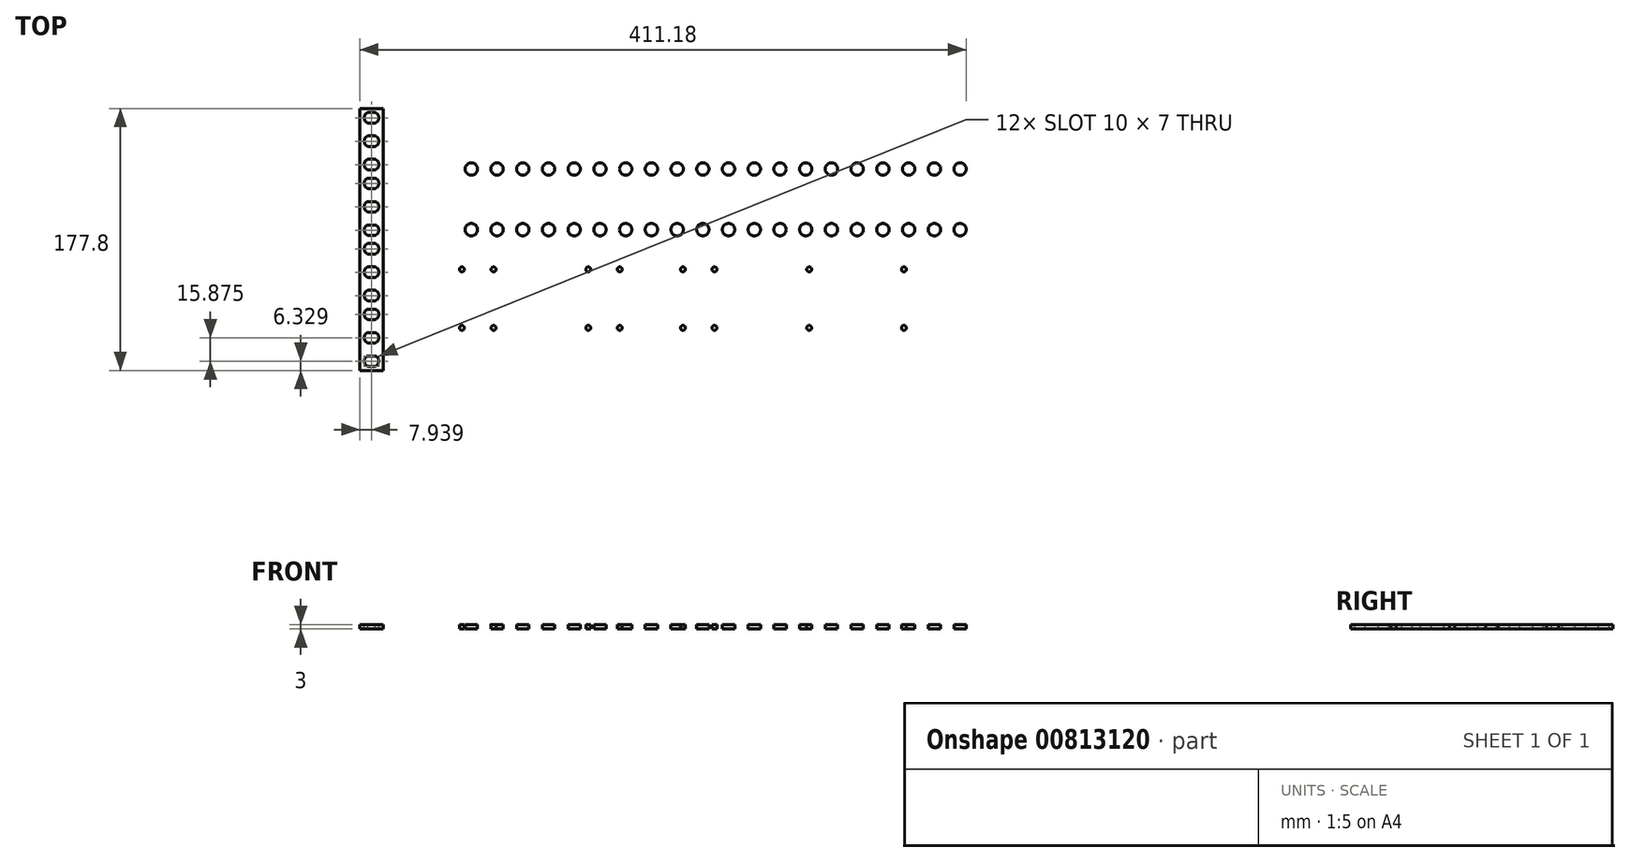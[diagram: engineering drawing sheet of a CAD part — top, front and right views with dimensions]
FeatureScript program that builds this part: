
annotation { "Feature Type Name" : "Feature", "Feature Type Description" : "" }
export const myFeature = defineFeature(function(context is Context, id is Id, definition is map)
    precondition{}
    {
        {
            var Q0;
            Q0=qCreatedBy(makeId("Top.planeOp"),FACE);
            var sketch = newSketch(context, id + "F0", { "sketchPlane" : qUnion([Q0])});
            skLineSegment(sketch, "E0.bottom", {"start": v(-66.95, 141.25) * mm, "end": v(415.65, 141.25) * mm});
            skLineSegment(sketch, "E0.top", {"start": v(-66.95, -36.55) * mm, "end": v(415.65, -36.55) * mm});
            skLineSegment(sketch, "E0.left", {"start": v(-66.95, 141.25) * mm, "end": v(-66.95, -36.55) * mm});
            skLineSegment(sketch, "E0.right", {"start": v(415.65, 141.25) * mm, "end": v(415.65, -36.55) * mm});
            skSolve(sketch);
        }
        {
            var Q0;
            Q0=makeQuery(id+"F0.imprint","IMPRINT",FACE,{"disambiguationData":[TD([[makeQuery(id+"F0.imprint","IMPRINT",EDGE,{"derivedFrom":sQuery(id+"F0.wireOp",EDGE,"E0.bottom")}),-1.0]])]});
            extrude(context, id + "F1", {"entities" : qUnion([Q0]), "depth" : 3 * mm, "offsetDistance" : 25 * mm});
        }
        {
            var Q0;
            Q0=makeQuery(id+"F1.opExtrude","CAP_FACE",FACE,{"disambiguationData":[OSD([sQuery(id+"F0.wireOp",EDGE,"E0.bottom"),sQuery(id+"F0.wireOp",EDGE,"E0.top"),sQuery(id+"F0.wireOp",EDGE,"E0.left"),sQuery(id+"F0.wireOp",EDGE,"E0.right")])],"isStart":false});
            var sketch = newSketch(context, id + "F2", { "sketchPlane" : qUnion([Q0])});
            skPoint(sketch, "E1", {"position": v(-59.01, 134.9) * mm});
            skPoint(sketch, "E2", {"position": v(-59.01, 119.02) * mm});
            skPoint(sketch, "E3", {"position": v(-59.01, 103.15) * mm});
            skPoint(sketch, "E4", {"position": v(8.67, 120.69) * mm});
            skPoint(sketch, "E5", {"position": v(26.1, 120.69) * mm});
            skPoint(sketch, "E6", {"position": v(43.55, 120.69) * mm});
            skPoint(sketch, "E7", {"position": v(60.99, 120.69) * mm});
            skPoint(sketch, "E8", {"position": v(78.43, 120.69) * mm});
            skPoint(sketch, "E9", {"position": v(95.87, 120.69) * mm});
            skPoint(sketch, "E10", {"position": v(113.3, 120.69) * mm});
            skPoint(sketch, "E11", {"position": v(130.75, 120.69) * mm});
            skPoint(sketch, "E12", {"position": v(148.19, 120.69) * mm});
            skPoint(sketch, "E13", {"position": v(165.63, 120.69) * mm});
            skPoint(sketch, "E14", {"position": v(183.07, 120.69) * mm});
            skPoint(sketch, "E15", {"position": v(200.5, 120.69) * mm});
            skPoint(sketch, "E16", {"position": v(217.95, 120.69) * mm});
            skPoint(sketch, "E17", {"position": v(235.39, 120.69) * mm});
            skPoint(sketch, "E18", {"position": v(252.83, 120.69) * mm});
            skPoint(sketch, "E19", {"position": v(270.27, 120.69) * mm});
            skPoint(sketch, "E20", {"position": v(287.7, 120.69) * mm});
            skPoint(sketch, "E21", {"position": v(305.15, 120.69) * mm});
            skPoint(sketch, "E22", {"position": v(322.59, 120.69) * mm});
            skPoint(sketch, "E23", {"position": v(340.03, 120.69) * mm});
            skCircle(sketch, "E24", {"center": v(8.67, 120.69) * mm, "radius": 4.2 * mm});
            skCircle(sketch, "E25", {"center": v(26.1, 120.69) * mm, "radius": 4.2 * mm});
            skCircle(sketch, "E26", {"center": v(43.55, 120.69) * mm, "radius": 4.2 * mm});
            skCircle(sketch, "E27", {"center": v(60.99, 120.69) * mm, "radius": 4.2 * mm});
            skCircle(sketch, "E28", {"center": v(78.43, 120.69) * mm, "radius": 4.2 * mm});
            skCircle(sketch, "E29", {"center": v(95.87, 120.69) * mm, "radius": 4.2 * mm});
            skCircle(sketch, "E30", {"center": v(113.3, 120.69) * mm, "radius": 4.2 * mm});
            skCircle(sketch, "E31", {"center": v(130.75, 120.69) * mm, "radius": 4.2 * mm});
            skCircle(sketch, "E32", {"center": v(148.19, 120.69) * mm, "radius": 4.2 * mm});
            skCircle(sketch, "E33", {"center": v(165.63, 120.69) * mm, "radius": 4.2 * mm});
            skCircle(sketch, "E34", {"center": v(183.07, 120.69) * mm, "radius": 4.2 * mm});
            skCircle(sketch, "E35", {"center": v(200.5, 120.69) * mm, "radius": 4.2 * mm});
            skCircle(sketch, "E36", {"center": v(217.95, 120.69) * mm, "radius": 4.2 * mm});
            skCircle(sketch, "E37", {"center": v(235.39, 120.69) * mm, "radius": 4.2 * mm});
            skCircle(sketch, "E38", {"center": v(252.83, 120.69) * mm, "radius": 4.2 * mm});
            skCircle(sketch, "E39", {"center": v(270.27, 120.69) * mm, "radius": 4.2 * mm});
            skCircle(sketch, "E40", {"center": v(287.7, 120.69) * mm, "radius": 4.2 * mm});
            skCircle(sketch, "E41", {"center": v(305.15, 120.69) * mm, "radius": 4.2 * mm});
            skCircle(sketch, "E42", {"center": v(340.03, 120.69) * mm, "radius": 4.2 * mm});
            skCircle(sketch, "E43", {"center": v(322.59, 120.69) * mm, "radius": 4.2 * mm});
            skLineSegment(sketch, "E44.MirrorCS", {"start": v(-59.01, 106.66) * mm, "end": v(-56.51, 106.66) * mm});
            skLineSegment(sketch, "E45.MirrorCS", {"start": v(-59.01, 106.66) * mm, "end": v(-61.51, 106.66) * mm});
            skLineSegment(sketch, "E46.MirrorCS", {"start": v(-59.01, 122.54) * mm, "end": v(-61.51, 122.54) * mm});
            skLineSegment(sketch, "E47.MirrorCS", {"start": v(-59.01, 115.54) * mm, "end": v(-61.51, 115.54) * mm});
            skLineSegment(sketch, "E48.MirrorCS", {"start": v(-59.01, 131.41) * mm, "end": v(-56.51, 131.41) * mm});
            skLineSegment(sketch, "E49.MirrorCS", {"start": v(-59.01, 99.66) * mm, "end": v(-61.51, 99.66) * mm});
            skLineSegment(sketch, "E50.MirrorCS", {"start": v(-59.01, 131.41) * mm, "end": v(-61.51, 131.41) * mm});
            skLineSegment(sketch, "E51.MirrorCS", {"start": v(-59.01, 138.41) * mm, "end": v(-56.51, 138.41) * mm});
            skLineSegment(sketch, "E52.MirrorCS", {"start": v(-59.01, 115.54) * mm, "end": v(-56.51, 115.54) * mm});
            skLineSegment(sketch, "E53.MirrorCS", {"start": v(-59.01, 99.66) * mm, "end": v(-56.51, 99.66) * mm});
            skLineSegment(sketch, "E54.MirrorCS", {"start": v(-59.01, 138.41) * mm, "end": v(-61.51, 138.41) * mm});
            skLineSegment(sketch, "E55.MirrorCS", {"start": v(-59.01, 122.54) * mm, "end": v(-56.51, 122.54) * mm});
            skArc(sketch, "E56.MirrorCS", {"start": v(-61.51, 122.54) * mm, "mid": v(-64.01, 119.04) * mm, "end": v(-61.51, 115.54) * mm});
            skArc(sketch, "E57.MirrorCS", {"start": v(-61.51, 99.66) * mm, "mid": v(-64.01, 103.16) * mm, "end": v(-61.51, 106.66) * mm});
            skArc(sketch, "E58.MirrorCS", {"start": v(-56.51, 106.66) * mm, "mid": v(-54.01, 103.16) * mm, "end": v(-56.51, 99.66) * mm});
            skPoint(sketch, "E59.MirrorP", {"position": v(-64.01, 103.15) * mm});
            skArc(sketch, "E60.MirrorCS", {"start": v(-61.51, 131.41) * mm, "mid": v(-64.01, 134.91) * mm, "end": v(-61.51, 138.41) * mm});
            skArc(sketch, "E61.MirrorCS", {"start": v(-56.51, 115.54) * mm, "mid": v(-54.01, 119.04) * mm, "end": v(-56.51, 122.54) * mm});
            skArc(sketch, "E62.MirrorCS", {"start": v(-56.51, 138.41) * mm, "mid": v(-54.01, 134.91) * mm, "end": v(-56.51, 131.41) * mm});
            skPoint(sketch, "E63", {"position": v(-40.48, 32.03) * mm});
            skPoint(sketch, "E64", {"position": v(-19.08, 32.03) * mm});
            skPoint(sketch, "E65", {"position": v(-19.08, -7.67) * mm});
            skCircle(sketch, "E66", {"center": v(-40.48, 32.03) * mm, "radius": 1.65 * mm});
            skCircle(sketch, "E67", {"center": v(-19.08, 32.03) * mm, "radius": 1.65 * mm});
            skCircle(sketch, "E68", {"center": v(-19.08, -7.67) * mm, "radius": 1.65 * mm});
            skCircle(sketch, "E69.MirrorC", {"center": v(2.32, 32.03) * mm, "radius": 1.65 * mm});
            skCircle(sketch, "E70.MirrorC", {"center": v(2.32, -7.67) * mm, "radius": 1.65 * mm});
            skCircle(sketch, "E71.MirrorC", {"center": v(23.72, 32.03) * mm, "radius": 1.65 * mm});
            skCircle(sketch, "E72.MirrorC", {"center": v(23.72, -7.67) * mm, "radius": 1.65 * mm});
            skPoint(sketch, "E73.MirrorP", {"position": v(45.12, 32.03) * mm});
            skCircle(sketch, "E74.MirrorC", {"center": v(45.12, -7.67) * mm, "radius": 1.65 * mm});
            skCircle(sketch, "E75.MirrorC", {"center": v(45.12, 32.03) * mm, "radius": 1.65 * mm});
            skPoint(sketch, "E76.MirrorP", {"position": v(66.52, -7.67) * mm});
            skPoint(sketch, "E77.MirrorP", {"position": v(66.52, 32.03) * mm});
            skCircle(sketch, "E78.MirrorC", {"center": v(66.52, -7.67) * mm, "radius": 1.65 * mm});
            skCircle(sketch, "E79.MirrorC", {"center": v(66.52, 32.03) * mm, "radius": 1.65 * mm});
            skPoint(sketch, "E80.MirrorP", {"position": v(87.92, -7.67) * mm});
            skCircle(sketch, "E81.MirrorC", {"center": v(87.92, 32.03) * mm, "radius": 1.65 * mm});
            skCircle(sketch, "E82.MirrorC", {"center": v(87.92, -7.67) * mm, "radius": 1.65 * mm});
            skCircle(sketch, "E83.MirrorC", {"center": v(109.32, 32.03) * mm, "radius": 1.65 * mm});
            skCircle(sketch, "E84.MirrorC", {"center": v(109.32, -7.67) * mm, "radius": 1.65 * mm});
            skCircle(sketch, "E85.MirrorC", {"center": v(194.92, -7.67) * mm, "radius": 1.65 * mm});
            skCircle(sketch, "E86.MirrorC", {"center": v(194.92, 32.03) * mm, "radius": 1.65 * mm});
            skCircle(sketch, "E87.MirrorC", {"center": v(152.12, -7.67) * mm, "radius": 1.65 * mm});
            skCircle(sketch, "E88.MirrorC", {"center": v(173.52, 32.03) * mm, "radius": 1.65 * mm});
            skCircle(sketch, "E89.MirrorC", {"center": v(216.32, -7.67) * mm, "radius": 1.65 * mm});
            skCircle(sketch, "E90.MirrorC", {"center": v(216.32, 32.03) * mm, "radius": 1.65 * mm});
            skCircle(sketch, "E91.MirrorC", {"center": v(173.52, -7.67) * mm, "radius": 1.65 * mm});
            skCircle(sketch, "E92.MirrorC", {"center": v(152.12, 32.03) * mm, "radius": 1.65 * mm});
            skCircle(sketch, "E93.MirrorC", {"center": v(130.72, -7.67) * mm, "radius": 1.65 * mm});
            skCircle(sketch, "E94.MirrorC", {"center": v(130.72, 32.03) * mm, "radius": 1.65 * mm});
            skCircle(sketch, "E95.MirrorC", {"center": v(280.52, 32.03) * mm, "radius": 1.65 * mm});
            skCircle(sketch, "E96.MirrorC", {"center": v(301.92, -7.67) * mm, "radius": 1.65 * mm});
            skCircle(sketch, "E97.MirrorC", {"center": v(301.92, 32.03) * mm, "radius": 1.65 * mm});
            skCircle(sketch, "E98.MirrorC", {"center": v(259.12, -7.67) * mm, "radius": 1.65 * mm});
            skCircle(sketch, "E99.MirrorC", {"center": v(237.72, 32.03) * mm, "radius": 1.65 * mm});
            skCircle(sketch, "E100.MirrorC", {"center": v(237.72, -7.67) * mm, "radius": 1.65 * mm});
            skCircle(sketch, "E101.MirrorC", {"center": v(323.32, 32.03) * mm, "radius": 1.65 * mm});
            skCircle(sketch, "E102.MirrorC", {"center": v(259.12, 32.03) * mm, "radius": 1.65 * mm});
            skCircle(sketch, "E103.MirrorC", {"center": v(280.52, -7.67) * mm, "radius": 1.65 * mm});
            skCircle(sketch, "E104.MirrorC", {"center": v(323.32, -7.67) * mm, "radius": 1.65 * mm});
            skCircle(sketch, "E105.MirrorC", {"center": v(344.72, -7.67) * mm, "radius": 1.65 * mm});
            skCircle(sketch, "E106.MirrorC", {"center": v(344.72, 32.03) * mm, "radius": 1.65 * mm});
            skCircle(sketch, "E107.MirrorC", {"center": v(364.25, 107.27) * mm, "radius": 1.65 * mm});
            skCircle(sketch, "E108.MirrorC", {"center": v(364.25, 67.57) * mm, "radius": 1.65 * mm});
            skCircle(sketch, "E109.MirrorC", {"center": v(385.65, 67.55) * mm, "radius": 1.65 * mm});
            skCircle(sketch, "E110.MirrorC", {"center": v(385.65, 107.25) * mm, "radius": 1.65 * mm});
            skCircle(sketch, "E111.MirrorC", {"center": v(-36.95, 107.25) * mm, "radius": 1.65 * mm});
            skCircle(sketch, "E112.MirrorC", {"center": v(-36.95, 67.55) * mm, "radius": 1.65 * mm});
            skCircle(sketch, "E113.MirrorC", {"center": v(-15.55, 67.55) * mm, "radius": 1.65 * mm});
            skCircle(sketch, "E114.MirrorC", {"center": v(-15.55, 107.25) * mm, "radius": 1.65 * mm});
            skPoint(sketch, "E115.MirrorP", {"position": v(26.1, 100.13) * mm});
            skPoint(sketch, "E116.MirrorP", {"position": v(8.67, 100.13) * mm});
            skPoint(sketch, "E117.MirrorP", {"position": v(340.03, 100.13) * mm});
            skCircle(sketch, "E118.MirrorC", {"center": v(183.07, 100.13) * mm, "radius": 4.2 * mm});
            skCircle(sketch, "E119.MirrorC", {"center": v(322.59, 100.13) * mm, "radius": 4.2 * mm});
            skPoint(sketch, "E120.MirrorP", {"position": v(78.43, 100.13) * mm});
            skCircle(sketch, "E121.MirrorC", {"center": v(252.83, 100.13) * mm, "radius": 4.2 * mm});
            skPoint(sketch, "E122.MirrorP", {"position": v(287.7, 100.13) * mm});
            skCircle(sketch, "E123.MirrorC", {"center": v(235.39, 100.13) * mm, "radius": 4.2 * mm});
            skPoint(sketch, "E124.MirrorP", {"position": v(43.55, 100.13) * mm});
            skCircle(sketch, "E125.MirrorC", {"center": v(60.99, 100.13) * mm, "radius": 4.2 * mm});
            skCircle(sketch, "E126.MirrorC", {"center": v(200.5, 100.13) * mm, "radius": 4.2 * mm});
            skPoint(sketch, "E127.MirrorP", {"position": v(148.19, 100.13) * mm});
            skCircle(sketch, "E128.MirrorC", {"center": v(43.55, 100.13) * mm, "radius": 4.2 * mm});
            skCircle(sketch, "E129.MirrorC", {"center": v(287.7, 100.13) * mm, "radius": 4.2 * mm});
            skCircle(sketch, "E130.MirrorC", {"center": v(165.63, 100.13) * mm, "radius": 4.2 * mm});
            skCircle(sketch, "E131.MirrorC", {"center": v(340.03, 100.13) * mm, "radius": 4.2 * mm});
            skCircle(sketch, "E132.MirrorC", {"center": v(305.15, 100.13) * mm, "radius": 4.2 * mm});
            skPoint(sketch, "E133.MirrorP", {"position": v(130.75, 100.13) * mm});
            skCircle(sketch, "E134.MirrorC", {"center": v(113.3, 100.13) * mm, "radius": 4.2 * mm});
            skPoint(sketch, "E135.MirrorP", {"position": v(270.27, 100.13) * mm});
            skPoint(sketch, "E136.MirrorP", {"position": v(217.95, 100.13) * mm});
            skCircle(sketch, "E137.MirrorC", {"center": v(8.67, 100.13) * mm, "radius": 4.2 * mm});
            skCircle(sketch, "E138.MirrorC", {"center": v(130.75, 100.13) * mm, "radius": 4.2 * mm});
            skCircle(sketch, "E139.MirrorC", {"center": v(78.43, 100.13) * mm, "radius": 4.2 * mm});
            skCircle(sketch, "E140.MirrorC", {"center": v(148.19, 100.13) * mm, "radius": 4.2 * mm});
            skCircle(sketch, "E141.MirrorC", {"center": v(26.1, 100.13) * mm, "radius": 4.2 * mm});
            skCircle(sketch, "E142.MirrorC", {"center": v(217.95, 100.13) * mm, "radius": 4.2 * mm});
            skCircle(sketch, "E143.MirrorC", {"center": v(270.27, 100.13) * mm, "radius": 4.2 * mm});
            skPoint(sketch, "E144.MirrorP", {"position": v(95.87, 100.13) * mm});
            skCircle(sketch, "E145.MirrorC", {"center": v(95.87, 100.13) * mm, "radius": 4.2 * mm});
            skCircle(sketch, "E146.MirrorC", {"center": v(8.67, 59) * mm, "radius": 4.2 * mm});
            skCircle(sketch, "E147.MirrorC", {"center": v(8.67, 79.57) * mm, "radius": 4.2 * mm});
            skCircle(sketch, "E148.MirrorC", {"center": v(26.1, 79.57) * mm, "radius": 4.2 * mm});
            skCircle(sketch, "E149.MirrorC", {"center": v(26.1, 59) * mm, "radius": 4.2 * mm});
            skCircle(sketch, "E150.MirrorC", {"center": v(270.27, 59) * mm, "radius": 4.2 * mm});
            skCircle(sketch, "E151.MirrorC", {"center": v(287.7, 79.57) * mm, "radius": 4.2 * mm});
            skCircle(sketch, "E152.MirrorC", {"center": v(148.19, 59) * mm, "radius": 4.2 * mm});
            skCircle(sketch, "E153.MirrorC", {"center": v(322.59, 79.57) * mm, "radius": 4.2 * mm});
            skCircle(sketch, "E154.MirrorC", {"center": v(43.55, 79.57) * mm, "radius": 4.2 * mm});
            skCircle(sketch, "E155.MirrorC", {"center": v(252.83, 79.57) * mm, "radius": 4.2 * mm});
            skCircle(sketch, "E156.MirrorC", {"center": v(95.87, 59) * mm, "radius": 4.2 * mm});
            skCircle(sketch, "E157.MirrorC", {"center": v(60.99, 79.57) * mm, "radius": 4.2 * mm});
            skCircle(sketch, "E158.MirrorC", {"center": v(183.07, 59) * mm, "radius": 4.2 * mm});
            skCircle(sketch, "E159.MirrorC", {"center": v(113.3, 79.57) * mm, "radius": 4.2 * mm});
            skCircle(sketch, "E160.MirrorC", {"center": v(148.19, 79.57) * mm, "radius": 4.2 * mm});
            skCircle(sketch, "E161.MirrorC", {"center": v(217.95, 79.57) * mm, "radius": 4.2 * mm});
            skCircle(sketch, "E162.MirrorC", {"center": v(200.5, 59) * mm, "radius": 4.2 * mm});
            skCircle(sketch, "E163.MirrorC", {"center": v(322.59, 59) * mm, "radius": 4.2 * mm});
            skCircle(sketch, "E164.MirrorC", {"center": v(95.87, 79.57) * mm, "radius": 4.2 * mm});
            skCircle(sketch, "E165.MirrorC", {"center": v(165.63, 79.57) * mm, "radius": 4.2 * mm});
            skCircle(sketch, "E166.MirrorC", {"center": v(78.43, 59) * mm, "radius": 4.2 * mm});
            skCircle(sketch, "E167.MirrorC", {"center": v(305.15, 79.57) * mm, "radius": 4.2 * mm});
            skCircle(sketch, "E168.MirrorC", {"center": v(60.99, 59) * mm, "radius": 4.2 * mm});
            skCircle(sketch, "E169.MirrorC", {"center": v(270.27, 79.57) * mm, "radius": 4.2 * mm});
            skCircle(sketch, "E170.MirrorC", {"center": v(113.3, 59) * mm, "radius": 4.2 * mm});
            skCircle(sketch, "E171.MirrorC", {"center": v(235.39, 59) * mm, "radius": 4.2 * mm});
            skCircle(sketch, "E172.MirrorC", {"center": v(235.39, 79.57) * mm, "radius": 4.2 * mm});
            skCircle(sketch, "E173.MirrorC", {"center": v(305.15, 59) * mm, "radius": 4.2 * mm});
            skCircle(sketch, "E174.MirrorC", {"center": v(200.5, 79.57) * mm, "radius": 4.2 * mm});
            skCircle(sketch, "E175.MirrorC", {"center": v(217.95, 59) * mm, "radius": 4.2 * mm});
            skCircle(sketch, "E176.MirrorC", {"center": v(43.55, 59) * mm, "radius": 4.2 * mm});
            skCircle(sketch, "E177.MirrorC", {"center": v(130.75, 59) * mm, "radius": 4.2 * mm});
            skCircle(sketch, "E178.MirrorC", {"center": v(340.03, 79.57) * mm, "radius": 4.2 * mm});
            skCircle(sketch, "E179.MirrorC", {"center": v(340.03, 59) * mm, "radius": 4.2 * mm});
            skCircle(sketch, "E180.MirrorC", {"center": v(78.43, 79.57) * mm, "radius": 4.2 * mm});
            skCircle(sketch, "E181.MirrorC", {"center": v(183.07, 79.57) * mm, "radius": 4.2 * mm});
            skCircle(sketch, "E182.MirrorC", {"center": v(165.63, 59) * mm, "radius": 4.2 * mm});
            skCircle(sketch, "E183.MirrorC", {"center": v(130.75, 79.57) * mm, "radius": 4.2 * mm});
            skCircle(sketch, "E184.MirrorC", {"center": v(287.7, 59) * mm, "radius": 4.2 * mm});
            skCircle(sketch, "E185.MirrorC", {"center": v(252.83, 59) * mm, "radius": 4.2 * mm});
            skLineSegment(sketch, "E186", {"start": v(-51.07, 141.25) * mm, "end": v(-51.07, -36.55) * mm});
            skLineSegment(sketch, "E187", {"start": v(-66.95, 96.8) * mm, "end": v(-51.07, 96.8) * mm});
            skLineSegment(sketch, "E188.MirrorCS", {"start": v(-59.01, 71.05) * mm, "end": v(-56.51, 71.05) * mm});
            skLineSegment(sketch, "E189.MirrorCS", {"start": v(-59.01, 93.93) * mm, "end": v(-61.51, 93.93) * mm});
            skLineSegment(sketch, "E190.MirrorCS", {"start": v(-59.01, 78.05) * mm, "end": v(-61.51, 78.05) * mm});
            skLineSegment(sketch, "E191.MirrorCS", {"start": v(-59.01, 93.93) * mm, "end": v(-56.51, 93.93) * mm});
            skLineSegment(sketch, "E192.MirrorCS", {"start": v(-59.01, 78.05) * mm, "end": v(-56.51, 78.05) * mm});
            skLineSegment(sketch, "E193.MirrorCS", {"start": v(-59.01, 71.05) * mm, "end": v(-61.51, 71.05) * mm});
            skLineSegment(sketch, "E194.MirrorCS", {"start": v(-59.01, 86.93) * mm, "end": v(-61.51, 86.93) * mm});
            skLineSegment(sketch, "E195.MirrorCS", {"start": v(-59.01, 62.18) * mm, "end": v(-56.51, 62.18) * mm});
            skLineSegment(sketch, "E196.MirrorCS", {"start": v(-59.01, 55.18) * mm, "end": v(-56.51, 55.18) * mm});
            skLineSegment(sketch, "E197.MirrorCS", {"start": v(-59.01, 55.18) * mm, "end": v(-61.51, 55.18) * mm});
            skLineSegment(sketch, "E198.MirrorCS", {"start": v(-59.01, 86.93) * mm, "end": v(-56.51, 86.93) * mm});
            skLineSegment(sketch, "E199.MirrorCS", {"start": v(-59.01, 62.18) * mm, "end": v(-61.51, 62.18) * mm});
            skArc(sketch, "E200.MirrorCS", {"start": v(-61.51, 71.05) * mm, "mid": v(-64.01, 74.55) * mm, "end": v(-61.51, 78.05) * mm});
            skPoint(sketch, "E201.MirrorP", {"position": v(-59.01, 90.45) * mm});
            skPoint(sketch, "E202.MirrorP", {"position": v(-59.01, 74.57) * mm});
            skArc(sketch, "E203.MirrorCS", {"start": v(-56.51, 78.05) * mm, "mid": v(-54.01, 74.55) * mm, "end": v(-56.51, 71.05) * mm});
            skArc(sketch, "E204.MirrorCS", {"start": v(-56.51, 55.18) * mm, "mid": v(-54.01, 58.68) * mm, "end": v(-56.51, 62.18) * mm});
            skArc(sketch, "E205.MirrorCS", {"start": v(-61.51, 62.18) * mm, "mid": v(-64.01, 58.68) * mm, "end": v(-61.51, 55.18) * mm});
            skArc(sketch, "E206.MirrorCS", {"start": v(-56.51, 86.93) * mm, "mid": v(-54.01, 90.43) * mm, "end": v(-56.51, 93.93) * mm});
            skArc(sketch, "E207.MirrorCS", {"start": v(-61.51, 93.93) * mm, "mid": v(-64.01, 90.43) * mm, "end": v(-61.51, 86.93) * mm});
            skPoint(sketch, "E208.MirrorP", {"position": v(-59.01, 58.7) * mm});
            skPoint(sketch, "E209.MirrorP", {"position": v(-64.01, 90.44) * mm});
            skLineSegment(sketch, "E210", {"start": v(-66.95, 52.35) * mm, "end": v(-51.07, 52.35) * mm});
            skLineSegment(sketch, "E211.MirrorCS", {"start": v(-59.01, 49.51) * mm, "end": v(-56.51, 49.51) * mm});
            skLineSegment(sketch, "E212.MirrorCS", {"start": v(-59.01, 33.64) * mm, "end": v(-61.51, 33.64) * mm});
            skLineSegment(sketch, "E213.MirrorCS", {"start": v(-59.01, -17.85) * mm, "end": v(-56.51, -17.85) * mm});
            skLineSegment(sketch, "E214.MirrorCS", {"start": v(-59.01, 10.76) * mm, "end": v(-61.51, 10.76) * mm});
            skLineSegment(sketch, "E215.MirrorCS", {"start": v(-59.01, 10.76) * mm, "end": v(-56.51, 10.76) * mm});
            skLineSegment(sketch, "E216.MirrorCS", {"start": v(-59.01, -26.72) * mm, "end": v(-56.51, -26.72) * mm});
            skLineSegment(sketch, "E217.MirrorCS", {"start": v(-59.01, 42.51) * mm, "end": v(-56.51, 42.51) * mm});
            skLineSegment(sketch, "E218.MirrorCS", {"start": v(-59.01, -33.72) * mm, "end": v(-56.51, -33.72) * mm});
            skLineSegment(sketch, "E219.MirrorCS", {"start": v(-59.01, -10.85) * mm, "end": v(-56.51, -10.85) * mm});
            skLineSegment(sketch, "E220.MirrorCS", {"start": v(-59.01, -10.85) * mm, "end": v(-61.51, -10.85) * mm});
            skLineSegment(sketch, "E221.MirrorCS", {"start": v(-59.01, 26.64) * mm, "end": v(-61.51, 26.64) * mm});
            skLineSegment(sketch, "E222.MirrorCS", {"start": v(-59.01, 17.76) * mm, "end": v(-56.51, 17.76) * mm});
            skLineSegment(sketch, "E223.MirrorCS", {"start": v(-59.01, -17.85) * mm, "end": v(-61.51, -17.85) * mm});
            skLineSegment(sketch, "E224.MirrorCS", {"start": v(-59.01, 42.51) * mm, "end": v(-61.51, 42.51) * mm});
            skLineSegment(sketch, "E225.MirrorCS", {"start": v(-59.01, 17.76) * mm, "end": v(-61.51, 17.76) * mm});
            skLineSegment(sketch, "E226.MirrorCS", {"start": v(-59.01, -33.72) * mm, "end": v(-61.51, -33.72) * mm});
            skLineSegment(sketch, "E227.MirrorCS", {"start": v(-59.01, 26.64) * mm, "end": v(-56.51, 26.64) * mm});
            skLineSegment(sketch, "E228.MirrorCS", {"start": v(-59.01, -1.97) * mm, "end": v(-56.51, -1.97) * mm});
            skPoint(sketch, "E229.MirrorP", {"position": v(-59.01, -14.33) * mm});
            skLineSegment(sketch, "E230.MirrorCS", {"start": v(-59.01, 49.51) * mm, "end": v(-61.51, 49.51) * mm});
            skPoint(sketch, "E231.MirrorP", {"position": v(-59.01, 30.12) * mm});
            skLineSegment(sketch, "E232.MirrorCS", {"start": v(-59.01, 5.03) * mm, "end": v(-56.51, 5.03) * mm});
            skLineSegment(sketch, "E233.MirrorCS", {"start": v(-59.01, -1.97) * mm, "end": v(-61.51, -1.97) * mm});
            skLineSegment(sketch, "E234.MirrorCS", {"start": v(-59.01, 33.64) * mm, "end": v(-56.51, 33.64) * mm});
            skPoint(sketch, "E235.MirrorP", {"position": v(-59.01, 14.25) * mm});
            skLineSegment(sketch, "E236.MirrorCS", {"start": v(-59.01, 5.03) * mm, "end": v(-61.51, 5.03) * mm});
            skPoint(sketch, "E237.MirrorP", {"position": v(-59.01, 1.55) * mm});
            skLineSegment(sketch, "E238.MirrorCS", {"start": v(-59.01, -26.72) * mm, "end": v(-61.51, -26.72) * mm});
            skArc(sketch, "E239.MirrorCS", {"start": v(-61.51, 10.76) * mm, "mid": v(-64.01, 14.26) * mm, "end": v(-61.51, 17.76) * mm});
            skArc(sketch, "E240.MirrorCS", {"start": v(-61.51, -17.85) * mm, "mid": v(-64.01, -14.35) * mm, "end": v(-61.51, -10.85) * mm});
            skPoint(sketch, "E241.MirrorP", {"position": v(-59.01, -30.2) * mm});
            skPoint(sketch, "E242.MirrorP", {"position": v(-59.01, 46) * mm});
            skArc(sketch, "E243.MirrorCS", {"start": v(-61.51, 5.03) * mm, "mid": v(-64.01, 1.53) * mm, "end": v(-61.51, -1.97) * mm});
            skArc(sketch, "E244.MirrorCS", {"start": v(-61.51, 33.64) * mm, "mid": v(-64.01, 30.14) * mm, "end": v(-61.51, 26.64) * mm});
            skPoint(sketch, "E245.MirrorP", {"position": v(-64.01, 14.25) * mm});
            skArc(sketch, "E246.MirrorCS", {"start": v(-56.51, -33.72) * mm, "mid": v(-54.01, -30.22) * mm, "end": v(-56.51, -26.72) * mm});
            skArc(sketch, "E247.MirrorCS", {"start": v(-56.51, 26.64) * mm, "mid": v(-54.01, 30.14) * mm, "end": v(-56.51, 33.64) * mm});
            skArc(sketch, "E248.MirrorCS", {"start": v(-61.51, -26.72) * mm, "mid": v(-64.01, -30.22) * mm, "end": v(-61.51, -33.72) * mm});
            skArc(sketch, "E249.MirrorCS", {"start": v(-61.51, 42.51) * mm, "mid": v(-64.01, 46.01) * mm, "end": v(-61.51, 49.51) * mm});
            skArc(sketch, "E250.MirrorCS", {"start": v(-56.51, -1.97) * mm, "mid": v(-54.01, 1.53) * mm, "end": v(-56.51, 5.03) * mm});
            skArc(sketch, "E251.MirrorCS", {"start": v(-56.51, -10.85) * mm, "mid": v(-54.01, -14.35) * mm, "end": v(-56.51, -17.85) * mm});
            skArc(sketch, "E252.MirrorCS", {"start": v(-56.51, 49.51) * mm, "mid": v(-54.01, 46.01) * mm, "end": v(-56.51, 42.51) * mm});
            skArc(sketch, "E253.MirrorCS", {"start": v(-56.51, 17.76) * mm, "mid": v(-54.01, 14.26) * mm, "end": v(-56.51, 10.76) * mm});
            skPoint(sketch, "E254.MirrorP", {"position": v(-64.01, 1.54) * mm});
            skLineSegment(sketch, "E255", {"start": v(174.35, 141.25) * mm, "end": v(174.35, -36.55) * mm});
            skLineSegment(sketch, "E256.MirrorCS", {"start": v(407.71, 93.93) * mm, "end": v(405.21, 93.93) * mm});
            skLineSegment(sketch, "E257.MirrorCS", {"start": v(407.71, -10.85) * mm, "end": v(405.21, -10.85) * mm});
            skArc(sketch, "E258.MirrorCS", {"start": v(410.21, 71.05) * mm, "mid": v(412.71, 74.55) * mm, "end": v(410.21, 78.05) * mm});
            skLineSegment(sketch, "E259.MirrorCS", {"start": v(407.71, 5.03) * mm, "end": v(410.21, 5.03) * mm});
            skLineSegment(sketch, "E260.MirrorCS", {"start": v(407.71, 26.64) * mm, "end": v(410.21, 26.64) * mm});
            skLineSegment(sketch, "E261.MirrorCS", {"start": v(407.71, 10.76) * mm, "end": v(410.21, 10.76) * mm});
            skLineSegment(sketch, "E262.MirrorCS", {"start": v(407.71, 78.05) * mm, "end": v(410.21, 78.05) * mm});
            skArc(sketch, "E263.MirrorCS", {"start": v(410.21, -17.85) * mm, "mid": v(412.71, -14.35) * mm, "end": v(410.21, -10.85) * mm});
            skLineSegment(sketch, "E264.MirrorCS", {"start": v(407.71, 55.18) * mm, "end": v(405.21, 55.18) * mm});
            skLineSegment(sketch, "E265.MirrorCS", {"start": v(407.71, 122.54) * mm, "end": v(405.21, 122.54) * mm});
            skLineSegment(sketch, "E266.MirrorCS", {"start": v(407.71, 17.76) * mm, "end": v(405.21, 17.76) * mm});
            skLineSegment(sketch, "E267.MirrorCS", {"start": v(407.71, 99.66) * mm, "end": v(410.21, 99.66) * mm});
            skArc(sketch, "E268.MirrorCS", {"start": v(410.21, 33.64) * mm, "mid": v(412.71, 30.14) * mm, "end": v(410.21, 26.64) * mm});
            skLineSegment(sketch, "E269.MirrorCS", {"start": v(407.71, 5.03) * mm, "end": v(405.21, 5.03) * mm});
            skLineSegment(sketch, "E270.MirrorCS", {"start": v(407.71, 115.54) * mm, "end": v(405.21, 115.54) * mm});
            skLineSegment(sketch, "E271.MirrorCS", {"start": v(407.71, -1.97) * mm, "end": v(405.21, -1.97) * mm});
            skLineSegment(sketch, "E272.MirrorCS", {"start": v(407.71, -1.97) * mm, "end": v(410.21, -1.97) * mm});
            skLineSegment(sketch, "E273.MirrorCS", {"start": v(407.71, 93.93) * mm, "end": v(410.21, 93.93) * mm});
            skLineSegment(sketch, "E274.MirrorCS", {"start": v(407.71, -17.85) * mm, "end": v(410.21, -17.85) * mm});
            skLineSegment(sketch, "E275.MirrorCS", {"start": v(407.71, 122.54) * mm, "end": v(410.21, 122.54) * mm});
            skLineSegment(sketch, "E276.MirrorCS", {"start": v(407.71, 17.76) * mm, "end": v(410.21, 17.76) * mm});
            skLineSegment(sketch, "E277.MirrorCS", {"start": v(407.71, 86.93) * mm, "end": v(405.21, 86.93) * mm});
            skLineSegment(sketch, "E278.MirrorCS", {"start": v(407.71, 78.05) * mm, "end": v(405.21, 78.05) * mm});
            skLineSegment(sketch, "E279.MirrorCS", {"start": v(407.71, 115.54) * mm, "end": v(410.21, 115.54) * mm});
            skLineSegment(sketch, "E280.MirrorCS", {"start": v(407.71, 106.66) * mm, "end": v(405.21, 106.66) * mm});
            skArc(sketch, "E281.MirrorCS", {"start": v(410.21, 122.54) * mm, "mid": v(412.71, 119.04) * mm, "end": v(410.21, 115.54) * mm});
            skLineSegment(sketch, "E282.MirrorCS", {"start": v(407.71, 106.66) * mm, "end": v(410.21, 106.66) * mm});
            skLineSegment(sketch, "E283.MirrorCS", {"start": v(407.71, 55.18) * mm, "end": v(410.21, 55.18) * mm});
            skLineSegment(sketch, "E284.MirrorCS", {"start": v(407.71, 99.66) * mm, "end": v(405.21, 99.66) * mm});
            skLineSegment(sketch, "E285.MirrorCS", {"start": v(407.71, 71.05) * mm, "end": v(405.21, 71.05) * mm});
            skLineSegment(sketch, "E286.MirrorCS", {"start": v(407.71, 71.05) * mm, "end": v(410.21, 71.05) * mm});
            skLineSegment(sketch, "E287.MirrorCS", {"start": v(407.71, 33.64) * mm, "end": v(405.21, 33.64) * mm});
            skLineSegment(sketch, "E288.MirrorCS", {"start": v(407.71, -17.85) * mm, "end": v(405.21, -17.85) * mm});
            skLineSegment(sketch, "E289.MirrorCS", {"start": v(407.71, 33.64) * mm, "end": v(410.21, 33.64) * mm});
            skLineSegment(sketch, "E290.MirrorCS", {"start": v(407.71, -10.85) * mm, "end": v(410.21, -10.85) * mm});
            skLineSegment(sketch, "E291.MirrorCS", {"start": v(407.71, 10.76) * mm, "end": v(405.21, 10.76) * mm});
            skLineSegment(sketch, "E292.MirrorCS", {"start": v(407.71, 26.64) * mm, "end": v(405.21, 26.64) * mm});
            skLineSegment(sketch, "E293.MirrorCS", {"start": v(407.71, 86.93) * mm, "end": v(410.21, 86.93) * mm});
            skLineSegment(sketch, "E294.MirrorCS", {"start": v(407.71, 42.51) * mm, "end": v(405.21, 42.51) * mm});
            skLineSegment(sketch, "E295.MirrorCS", {"start": v(407.71, 138.41) * mm, "end": v(405.21, 138.41) * mm});
            skPoint(sketch, "E296.MirrorP", {"position": v(407.71, -14.33) * mm});
            skPoint(sketch, "E297.MirrorP", {"position": v(407.71, 1.55) * mm});
            skPoint(sketch, "E298.MirrorP", {"position": v(407.71, 30.12) * mm});
            skPoint(sketch, "E299.MirrorP", {"position": v(407.71, 90.45) * mm});
            skPoint(sketch, "E300.MirrorP", {"position": v(407.71, 74.57) * mm});
            skLineSegment(sketch, "E301.MirrorCS", {"start": v(407.71, 138.41) * mm, "end": v(410.21, 138.41) * mm});
            skLineSegment(sketch, "E302.MirrorCS", {"start": v(407.71, 131.41) * mm, "end": v(410.21, 131.41) * mm});
            skLineSegment(sketch, "E303.MirrorCS", {"start": v(407.71, -33.72) * mm, "end": v(410.21, -33.72) * mm});
            skLineSegment(sketch, "E304.MirrorCS", {"start": v(407.71, 131.41) * mm, "end": v(405.21, 131.41) * mm});
            skArc(sketch, "E305.MirrorCS", {"start": v(410.21, 99.66) * mm, "mid": v(412.71, 103.16) * mm, "end": v(410.21, 106.66) * mm});
            skLineSegment(sketch, "E306.MirrorCS", {"start": v(407.71, -26.72) * mm, "end": v(410.21, -26.72) * mm});
            skPoint(sketch, "E307.MirrorP", {"position": v(407.71, 103.15) * mm});
            skLineSegment(sketch, "E308.MirrorCS", {"start": v(407.71, 42.51) * mm, "end": v(410.21, 42.51) * mm});
            skArc(sketch, "E309.MirrorCS", {"start": v(410.21, 5.03) * mm, "mid": v(412.71, 1.53) * mm, "end": v(410.21, -1.97) * mm});
            skLineSegment(sketch, "E310.MirrorCS", {"start": v(407.71, 49.51) * mm, "end": v(405.21, 49.51) * mm});
            skArc(sketch, "E311.MirrorCS", {"start": v(410.21, 10.76) * mm, "mid": v(412.71, 14.26) * mm, "end": v(410.21, 17.76) * mm});
            skLineSegment(sketch, "E312.MirrorCS", {"start": v(407.71, 49.51) * mm, "end": v(410.21, 49.51) * mm});
            skPoint(sketch, "E313.MirrorP", {"position": v(407.71, 119.02) * mm});
            skLineSegment(sketch, "E314.MirrorCS", {"start": v(407.71, 62.18) * mm, "end": v(410.21, 62.18) * mm});
            skLineSegment(sketch, "E315.MirrorCS", {"start": v(407.71, 62.18) * mm, "end": v(405.21, 62.18) * mm});
            skLineSegment(sketch, "E316.MirrorCS", {"start": v(407.71, -26.72) * mm, "end": v(405.21, -26.72) * mm});
            skArc(sketch, "E317.MirrorCS", {"start": v(410.21, 93.93) * mm, "mid": v(412.71, 90.43) * mm, "end": v(410.21, 86.93) * mm});
            skLineSegment(sketch, "E318.MirrorCS", {"start": v(407.71, -33.72) * mm, "end": v(405.21, -33.72) * mm});
            skPoint(sketch, "E319.MirrorP", {"position": v(407.71, 14.25) * mm});
            skPoint(sketch, "E320.MirrorP", {"position": v(407.71, 58.7) * mm});
            skPoint(sketch, "E321.MirrorP", {"position": v(412.71, 103.15) * mm});
            skArc(sketch, "E322.MirrorCS", {"start": v(405.21, -33.72) * mm, "mid": v(402.71, -30.22) * mm, "end": v(405.21, -26.72) * mm});
            skArc(sketch, "E323.MirrorCS", {"start": v(410.21, -26.72) * mm, "mid": v(412.71, -30.22) * mm, "end": v(410.21, -33.72) * mm});
            skPoint(sketch, "E324.MirrorP", {"position": v(407.71, 134.9) * mm});
            skArc(sketch, "E325.MirrorCS", {"start": v(405.21, 138.41) * mm, "mid": v(402.71, 134.91) * mm, "end": v(405.21, 131.41) * mm});
            skArc(sketch, "E326.MirrorCS", {"start": v(405.21, 17.76) * mm, "mid": v(402.71, 14.26) * mm, "end": v(405.21, 10.76) * mm});
            skArc(sketch, "E327.MirrorCS", {"start": v(405.21, -1.97) * mm, "mid": v(402.71, 1.53) * mm, "end": v(405.21, 5.03) * mm});
            skArc(sketch, "E328.MirrorCS", {"start": v(410.21, 62.18) * mm, "mid": v(412.71, 58.68) * mm, "end": v(410.21, 55.18) * mm});
            skArc(sketch, "E329.MirrorCS", {"start": v(405.21, 55.18) * mm, "mid": v(402.71, 58.68) * mm, "end": v(405.21, 62.18) * mm});
            skPoint(sketch, "E330.MirrorP", {"position": v(407.71, -30.2) * mm});
            skArc(sketch, "E331.MirrorCS", {"start": v(410.21, 131.41) * mm, "mid": v(412.71, 134.91) * mm, "end": v(410.21, 138.41) * mm});
            skArc(sketch, "E332.MirrorCS", {"start": v(405.21, -10.85) * mm, "mid": v(402.71, -14.35) * mm, "end": v(405.21, -17.85) * mm});
            skArc(sketch, "E333.MirrorCS", {"start": v(410.21, 42.51) * mm, "mid": v(412.71, 46.01) * mm, "end": v(410.21, 49.51) * mm});
            skArc(sketch, "E334.MirrorCS", {"start": v(405.21, 78.05) * mm, "mid": v(402.71, 74.55) * mm, "end": v(405.21, 71.05) * mm});
            skArc(sketch, "E335.MirrorCS", {"start": v(405.21, 106.66) * mm, "mid": v(402.71, 103.16) * mm, "end": v(405.21, 99.66) * mm});
            skPoint(sketch, "E336.MirrorP", {"position": v(412.71, 90.44) * mm});
            skPoint(sketch, "E337.MirrorP", {"position": v(407.71, 46) * mm});
            skArc(sketch, "E338.MirrorCS", {"start": v(405.21, 49.51) * mm, "mid": v(402.71, 46.01) * mm, "end": v(405.21, 42.51) * mm});
            skArc(sketch, "E339.MirrorCS", {"start": v(405.21, 115.54) * mm, "mid": v(402.71, 119.04) * mm, "end": v(405.21, 122.54) * mm});
            skPoint(sketch, "E340.MirrorP", {"position": v(412.71, 1.54) * mm});
            skPoint(sketch, "E341.MirrorP", {"position": v(412.71, 14.25) * mm});
            skArc(sketch, "E342.MirrorCS", {"start": v(405.21, 26.64) * mm, "mid": v(402.71, 30.14) * mm, "end": v(405.21, 33.64) * mm});
            skArc(sketch, "E343.MirrorCS", {"start": v(405.21, 86.93) * mm, "mid": v(402.71, 90.43) * mm, "end": v(405.21, 93.93) * mm});
            skSolve(sketch);
        }
        {
            var Q0;
            Q0=makeQuery(id+"F2.imprint","IMPRINT",FACE,{"disambiguationData":[TD([[makeQuery(id+"F2.imprint","IMPRINT",EDGE,{"derivedFrom":sQuery(id+"F2.wireOp",EDGE,"6KtdoT9x-rWsy-FY7Z-YWYD-vtVlDtfl7iPq")}),1.0]])]});
            var sketch = newSketch(context, id + "F3", { "sketchPlane" : qUnion([Q0])});
            skSolve(sketch);
        }
        {
            var Q0;
            Q0=makeQuery(id+"F3.imprint","IMPRINT",FACE,{"disambiguationData":[TD([[makeQuery(id+"F3.imprint","IMPRINT",EDGE,{"derivedFrom":makeQuery(id+"F2.imprint","IMPRINT",EDGE,{"derivedFrom":sQuery(id+"F2.wireOp",EDGE,"E48.MirrorCS")})}),1.0]])]});
            var Q1;
            Q1=makeQuery(id+"F3.imprint","IMPRINT",FACE,{"disambiguationData":[TD([[makeQuery(id+"F3.imprint","IMPRINT",EDGE,{"derivedFrom":makeQuery(id+"F2.imprint","IMPRINT",EDGE,{"derivedFrom":sQuery(id+"F2.wireOp",EDGE,"E30")})}),1.0]])]});
            var Q2;
            Q2=makeQuery(id+"F3.imprint","IMPRINT",FACE,{"disambiguationData":[TD([[makeQuery(id+"F3.imprint","IMPRINT",EDGE,{"derivedFrom":makeQuery(id+"F2.imprint","IMPRINT",EDGE,{"derivedFrom":sQuery(id+"F2.wireOp",EDGE,"E43")})}),1.0]])]});
            var Q3;
            Q3=makeQuery(id+"F3.imprint","IMPRINT",FACE,{"disambiguationData":[TD([[makeQuery(id+"F3.imprint","IMPRINT",EDGE,{"derivedFrom":makeQuery(id+"F2.imprint","IMPRINT",EDGE,{"derivedFrom":sQuery(id+"F2.wireOp",EDGE,"E25")})}),1.0]])]});
            var Q4;
            Q4=makeQuery(id+"F3.imprint","IMPRINT",FACE,{"disambiguationData":[TD([[makeQuery(id+"F3.imprint","IMPRINT",EDGE,{"derivedFrom":makeQuery(id+"F2.imprint","IMPRINT",EDGE,{"derivedFrom":sQuery(id+"F2.wireOp",EDGE,"E31")})}),1.0]])]});
            var Q5;
            Q5=makeQuery(id+"F3.imprint","IMPRINT",FACE,{"disambiguationData":[TD([[makeQuery(id+"F3.imprint","IMPRINT",EDGE,{"derivedFrom":makeQuery(id+"F2.imprint","IMPRINT",EDGE,{"derivedFrom":sQuery(id+"F2.wireOp",EDGE,"E39")})}),1.0]])]});
            var Q6;
            Q6=makeQuery(id+"F3.imprint","IMPRINT",FACE,{"disambiguationData":[TD([[makeQuery(id+"F3.imprint","IMPRINT",EDGE,{"derivedFrom":makeQuery(id+"F2.imprint","IMPRINT",EDGE,{"derivedFrom":sQuery(id+"F2.wireOp",EDGE,"E27")})}),1.0]])]});
            var Q7;
            Q7=makeQuery(id+"F3.imprint","IMPRINT",FACE,{"disambiguationData":[TD([[makeQuery(id+"F3.imprint","IMPRINT",EDGE,{"derivedFrom":makeQuery(id+"F2.imprint","IMPRINT",EDGE,{"derivedFrom":sQuery(id+"F2.wireOp",EDGE,"E34")})}),1.0]])]});
            var Q8;
            Q8=makeQuery(id+"F3.imprint","IMPRINT",FACE,{"disambiguationData":[TD([[makeQuery(id+"F3.imprint","IMPRINT",EDGE,{"derivedFrom":makeQuery(id+"F2.imprint","IMPRINT",EDGE,{"derivedFrom":sQuery(id+"F2.wireOp",EDGE,"E40")})}),1.0]])]});
            var Q9;
            Q9=makeQuery(id+"F3.imprint","IMPRINT",FACE,{"disambiguationData":[TD([[makeQuery(id+"F3.imprint","IMPRINT",EDGE,{"derivedFrom":makeQuery(id+"F2.imprint","IMPRINT",EDGE,{"derivedFrom":sQuery(id+"F2.wireOp",EDGE,"E28")})}),1.0]])]});
            var Q10;
            Q10=makeQuery(id+"F3.imprint","IMPRINT",FACE,{"disambiguationData":[TD([[makeQuery(id+"F3.imprint","IMPRINT",EDGE,{"derivedFrom":makeQuery(id+"F2.imprint","IMPRINT",EDGE,{"derivedFrom":sQuery(id+"F2.wireOp",EDGE,"E42")})}),1.0]])]});
            var Q11;
            Q11=makeQuery(id+"F3.imprint","IMPRINT",FACE,{"disambiguationData":[TD([[makeQuery(id+"F3.imprint","IMPRINT",EDGE,{"derivedFrom":makeQuery(id+"F2.imprint","IMPRINT",EDGE,{"derivedFrom":sQuery(id+"F2.wireOp",EDGE,"E32")})}),1.0]])]});
            var Q12;
            Q12=makeQuery(id+"F3.imprint","IMPRINT",FACE,{"disambiguationData":[TD([[makeQuery(id+"F3.imprint","IMPRINT",EDGE,{"derivedFrom":makeQuery(id+"F2.imprint","IMPRINT",EDGE,{"derivedFrom":sQuery(id+"F2.wireOp",EDGE,"E24")})}),1.0]])]});
            var Q13;
            Q13=makeQuery(id+"F3.imprint","IMPRINT",FACE,{"disambiguationData":[TD([[makeQuery(id+"F3.imprint","IMPRINT",EDGE,{"derivedFrom":makeQuery(id+"F2.imprint","IMPRINT",EDGE,{"derivedFrom":sQuery(id+"F2.wireOp",EDGE,"E26")})}),1.0]])]});
            var Q14;
            Q14=makeQuery(id+"F3.imprint","IMPRINT",FACE,{"disambiguationData":[TD([[makeQuery(id+"F3.imprint","IMPRINT",EDGE,{"derivedFrom":makeQuery(id+"F2.imprint","IMPRINT",EDGE,{"derivedFrom":sQuery(id+"F2.wireOp",EDGE,"E33")})}),1.0]])]});
            var Q15;
            Q15=makeQuery(id+"F3.imprint","IMPRINT",FACE,{"disambiguationData":[TD([[makeQuery(id+"F3.imprint","IMPRINT",EDGE,{"derivedFrom":makeQuery(id+"F2.imprint","IMPRINT",EDGE,{"derivedFrom":sQuery(id+"F2.wireOp",EDGE,"E29")})}),1.0]])]});
            var Q16;
            Q16=makeQuery(id+"F3.imprint","IMPRINT",FACE,{"disambiguationData":[TD([[makeQuery(id+"F3.imprint","IMPRINT",EDGE,{"derivedFrom":makeQuery(id+"F2.imprint","IMPRINT",EDGE,{"derivedFrom":sQuery(id+"F2.wireOp",EDGE,"E38")})}),1.0]])]});
            var Q17;
            Q17=makeQuery(id+"F3.imprint","IMPRINT",FACE,{"disambiguationData":[TD([[makeQuery(id+"F3.imprint","IMPRINT",EDGE,{"derivedFrom":makeQuery(id+"F2.imprint","IMPRINT",EDGE,{"derivedFrom":sQuery(id+"F2.wireOp",EDGE,"E36")})}),1.0]])]});
            var Q18;
            Q18=makeQuery(id+"F3.imprint","IMPRINT",FACE,{"disambiguationData":[TD([[makeQuery(id+"F3.imprint","IMPRINT",EDGE,{"derivedFrom":makeQuery(id+"F2.imprint","IMPRINT",EDGE,{"derivedFrom":sQuery(id+"F2.wireOp",EDGE,"E41")})}),1.0]])]});
            var Q19;
            Q19=makeQuery(id+"F3.imprint","IMPRINT",FACE,{"disambiguationData":[TD([[makeQuery(id+"F3.imprint","IMPRINT",EDGE,{"derivedFrom":makeQuery(id+"F2.imprint","IMPRINT",EDGE,{"derivedFrom":sQuery(id+"F2.wireOp",EDGE,"E37")})}),1.0]])]});
            var Q20;
            Q20=makeQuery(id+"F3.imprint","IMPRINT",FACE,{"disambiguationData":[TD([[makeQuery(id+"F3.imprint","IMPRINT",EDGE,{"derivedFrom":makeQuery(id+"F2.imprint","IMPRINT",EDGE,{"derivedFrom":sQuery(id+"F2.wireOp",EDGE,"E35")})}),1.0]])]});
            var Q21;
            Q21=makeQuery(id+"F2.imprint","IMPRINT",FACE,{"disambiguationData":[TD([[makeQuery(id+"F2.imprint","IMPRINT",EDGE,{"derivedFrom":sQuery(id+"F2.wireOp",EDGE,"E43")}),1.0]])]});
            var Q22;
            Q22=makeQuery(id+"F2.imprint","IMPRINT",FACE,{"disambiguationData":[TD([[makeQuery(id+"F2.imprint","IMPRINT",EDGE,{"derivedFrom":sQuery(id+"F2.wireOp",EDGE,"E41")}),1.0]])]});
            var Q23;
            Q23=makeQuery(id+"F2.imprint","IMPRINT",FACE,{"disambiguationData":[TD([[makeQuery(id+"F2.imprint","IMPRINT",EDGE,{"derivedFrom":sQuery(id+"F2.wireOp",EDGE,"E37")}),1.0]])]});
            var Q24;
            Q24=makeQuery(id+"F2.imprint","IMPRINT",FACE,{"disambiguationData":[TD([[makeQuery(id+"F2.imprint","IMPRINT",EDGE,{"derivedFrom":sQuery(id+"F2.wireOp",EDGE,"E33")}),1.0]])]});
            var Q25;
            Q25=makeQuery(id+"F2.imprint","IMPRINT",FACE,{"disambiguationData":[TD([[makeQuery(id+"F2.imprint","IMPRINT",EDGE,{"derivedFrom":sQuery(id+"F2.wireOp",EDGE,"E42")}),1.0]])]});
            var Q26;
            Q26=makeQuery(id+"F2.imprint","IMPRINT",FACE,{"disambiguationData":[TD([[makeQuery(id+"F2.imprint","IMPRINT",EDGE,{"derivedFrom":sQuery(id+"F2.wireOp",EDGE,"E25")}),1.0]])]});
            var Q27;
            Q27=makeQuery(id+"F2.imprint","IMPRINT",FACE,{"disambiguationData":[TD([[makeQuery(id+"F2.imprint","IMPRINT",EDGE,{"derivedFrom":sQuery(id+"F2.wireOp",EDGE,"E24")}),1.0]])]});
            var Q28;
            Q28=makeQuery(id+"F2.imprint","IMPRINT",FACE,{"disambiguationData":[TD([[makeQuery(id+"F2.imprint","IMPRINT",EDGE,{"derivedFrom":sQuery(id+"F2.wireOp",EDGE,"E40")}),1.0]])]});
            var Q29;
            Q29=makeQuery(id+"F2.imprint","IMPRINT",FACE,{"disambiguationData":[TD([[makeQuery(id+"F2.imprint","IMPRINT",EDGE,{"derivedFrom":sQuery(id+"F2.wireOp",EDGE,"E32")}),1.0]])]});
            var Q30;
            Q30=makeQuery(id+"F2.imprint","IMPRINT",FACE,{"disambiguationData":[TD([[makeQuery(id+"F2.imprint","IMPRINT",EDGE,{"derivedFrom":sQuery(id+"F2.wireOp",EDGE,"E35")}),1.0]])]});
            var Q31;
            Q31=makeQuery(id+"F2.imprint","IMPRINT",FACE,{"disambiguationData":[TD([[makeQuery(id+"F2.imprint","IMPRINT",EDGE,{"derivedFrom":sQuery(id+"F2.wireOp",EDGE,"E30")}),1.0]])]});
            var Q32;
            Q32=makeQuery(id+"F2.imprint","IMPRINT",FACE,{"disambiguationData":[TD([[makeQuery(id+"F2.imprint","IMPRINT",EDGE,{"derivedFrom":sQuery(id+"F2.wireOp",EDGE,"E29")}),1.0]])]});
            var Q33;
            Q33=makeQuery(id+"F2.imprint","IMPRINT",FACE,{"disambiguationData":[TD([[makeQuery(id+"F2.imprint","IMPRINT",EDGE,{"derivedFrom":sQuery(id+"F2.wireOp",EDGE,"E39")}),1.0]])]});
            var Q34;
            Q34=makeQuery(id+"F2.imprint","IMPRINT",FACE,{"disambiguationData":[TD([[makeQuery(id+"F2.imprint","IMPRINT",EDGE,{"derivedFrom":sQuery(id+"F2.wireOp",EDGE,"E27")}),1.0]])]});
            var Q35;
            Q35=makeQuery(id+"F2.imprint","IMPRINT",FACE,{"disambiguationData":[TD([[makeQuery(id+"F2.imprint","IMPRINT",EDGE,{"derivedFrom":sQuery(id+"F2.wireOp",EDGE,"E38")}),1.0]])]});
            var Q36;
            Q36=makeQuery(id+"F2.imprint","IMPRINT",FACE,{"disambiguationData":[TD([[makeQuery(id+"F2.imprint","IMPRINT",EDGE,{"derivedFrom":sQuery(id+"F2.wireOp",EDGE,"E28")}),1.0]])]});
            var Q37;
            Q37=makeQuery(id+"F2.imprint","IMPRINT",FACE,{"disambiguationData":[TD([[makeQuery(id+"F2.imprint","IMPRINT",EDGE,{"derivedFrom":sQuery(id+"F2.wireOp",EDGE,"E26")}),1.0]])]});
            var Q38;
            Q38=makeQuery(id+"F2.imprint","IMPRINT",FACE,{"disambiguationData":[TD([[makeQuery(id+"F2.imprint","IMPRINT",EDGE,{"derivedFrom":sQuery(id+"F2.wireOp",EDGE,"E31")}),1.0]])]});
            var Q39;
            Q39=makeQuery(id+"F2.imprint","IMPRINT",FACE,{"disambiguationData":[TD([[makeQuery(id+"F2.imprint","IMPRINT",EDGE,{"derivedFrom":sQuery(id+"F2.wireOp",EDGE,"E36")}),1.0]])]});
            var Q40;
            Q40=makeQuery(id+"F2.imprint","IMPRINT",FACE,{"disambiguationData":[TD([[makeQuery(id+"F2.imprint","IMPRINT",EDGE,{"derivedFrom":sQuery(id+"F2.wireOp",EDGE,"E34")}),1.0]])]});
            var Q41;
            Q41=makeQuery(id+"F3.imprint","IMPRINT",FACE,{"disambiguationData":[TD([[makeQuery(id+"F3.imprint","IMPRINT",EDGE,{"derivedFrom":makeQuery(id+"F2.imprint","IMPRINT",EDGE,{"derivedFrom":sQuery(id+"F2.wireOp",EDGE,"E107.MirrorC")})}),1.0]])]});
            var Q42;
            Q42=makeQuery(id+"F3.imprint","IMPRINT",FACE,{"disambiguationData":[TD([[makeQuery(id+"F3.imprint","IMPRINT",EDGE,{"derivedFrom":makeQuery(id+"F2.imprint","IMPRINT",EDGE,{"derivedFrom":sQuery(id+"F2.wireOp",EDGE,"E88.MirrorC")})}),-1.0]])]});
            var Q43;
            Q43=makeQuery(id+"F3.imprint","IMPRINT",FACE,{"disambiguationData":[TD([[makeQuery(id+"F3.imprint","IMPRINT",EDGE,{"derivedFrom":makeQuery(id+"F2.imprint","IMPRINT",EDGE,{"derivedFrom":sQuery(id+"F2.wireOp",EDGE,"E67")})}),1.0]])]});
            var Q44;
            Q44=makeQuery(id+"F3.imprint","IMPRINT",FACE,{"disambiguationData":[TD([[makeQuery(id+"F3.imprint","IMPRINT",EDGE,{"derivedFrom":makeQuery(id+"F2.imprint","IMPRINT",EDGE,{"derivedFrom":sQuery(id+"F2.wireOp",EDGE,"E74.MirrorC")})}),1.0]])]});
            var Q45;
            Q45=makeQuery(id+"F3.imprint","IMPRINT",FACE,{"disambiguationData":[TD([[makeQuery(id+"F3.imprint","IMPRINT",EDGE,{"derivedFrom":makeQuery(id+"F2.imprint","IMPRINT",EDGE,{"derivedFrom":sQuery(id+"F2.wireOp",EDGE,"E99.MirrorC")})}),-1.0]])]});
            var Q46;
            Q46=makeQuery(id+"F3.imprint","IMPRINT",FACE,{"disambiguationData":[TD([[makeQuery(id+"F3.imprint","IMPRINT",EDGE,{"derivedFrom":makeQuery(id+"F2.imprint","IMPRINT",EDGE,{"derivedFrom":sQuery(id+"F2.wireOp",EDGE,"E91.MirrorC")})}),-1.0]])]});
            var Q47;
            Q47=makeQuery(id+"F3.imprint","IMPRINT",FACE,{"disambiguationData":[TD([[makeQuery(id+"F3.imprint","IMPRINT",EDGE,{"derivedFrom":makeQuery(id+"F2.imprint","IMPRINT",EDGE,{"derivedFrom":sQuery(id+"F2.wireOp",EDGE,"E97.MirrorC")})}),-1.0]])]});
            var Q48;
            Q48=makeQuery(id+"F3.imprint","IMPRINT",FACE,{"disambiguationData":[TD([[makeQuery(id+"F3.imprint","IMPRINT",EDGE,{"derivedFrom":makeQuery(id+"F2.imprint","IMPRINT",EDGE,{"derivedFrom":sQuery(id+"F2.wireOp",EDGE,"E104.MirrorC")})}),1.0]])]});
            var Q49;
            Q49=makeQuery(id+"F3.imprint","IMPRINT",FACE,{"disambiguationData":[TD([[makeQuery(id+"F3.imprint","IMPRINT",EDGE,{"derivedFrom":makeQuery(id+"F2.imprint","IMPRINT",EDGE,{"derivedFrom":sQuery(id+"F2.wireOp",EDGE,"E103.MirrorC")})}),1.0]])]});
            var Q50;
            Q50=makeQuery(id+"F3.imprint","IMPRINT",FACE,{"disambiguationData":[TD([[makeQuery(id+"F3.imprint","IMPRINT",EDGE,{"derivedFrom":makeQuery(id+"F2.imprint","IMPRINT",EDGE,{"derivedFrom":sQuery(id+"F2.wireOp",EDGE,"E95.MirrorC")})}),1.0]])]});
            var Q51;
            Q51=makeQuery(id+"F3.imprint","IMPRINT",FACE,{"disambiguationData":[TD([[makeQuery(id+"F3.imprint","IMPRINT",EDGE,{"derivedFrom":makeQuery(id+"F2.imprint","IMPRINT",EDGE,{"derivedFrom":sQuery(id+"F2.wireOp",EDGE,"E101.MirrorC")})}),1.0]])]});
            var Q52;
            Q52=makeQuery(id+"F3.imprint","IMPRINT",FACE,{"disambiguationData":[TD([[makeQuery(id+"F3.imprint","IMPRINT",EDGE,{"derivedFrom":makeQuery(id+"F2.imprint","IMPRINT",EDGE,{"derivedFrom":sQuery(id+"F2.wireOp",EDGE,"E75.MirrorC")})}),1.0]])]});
            var Q53;
            Q53=makeQuery(id+"F3.imprint","IMPRINT",FACE,{"disambiguationData":[TD([[makeQuery(id+"F3.imprint","IMPRINT",EDGE,{"derivedFrom":makeQuery(id+"F2.imprint","IMPRINT",EDGE,{"derivedFrom":sQuery(id+"F2.wireOp",EDGE,"E82.MirrorC")})}),-1.0]])]});
            var Q54;
            Q54=makeQuery(id+"F3.imprint","IMPRINT",FACE,{"disambiguationData":[TD([[makeQuery(id+"F3.imprint","IMPRINT",EDGE,{"derivedFrom":makeQuery(id+"F2.imprint","IMPRINT",EDGE,{"derivedFrom":sQuery(id+"F2.wireOp",EDGE,"E92.MirrorC")})}),-1.0]])]});
            var Q55;
            Q55=makeQuery(id+"F3.imprint","IMPRINT",FACE,{"disambiguationData":[TD([[makeQuery(id+"F3.imprint","IMPRINT",EDGE,{"derivedFrom":makeQuery(id+"F2.imprint","IMPRINT",EDGE,{"derivedFrom":sQuery(id+"F2.wireOp",EDGE,"E100.MirrorC")})}),-1.0]])]});
            var Q56;
            Q56=makeQuery(id+"F3.imprint","IMPRINT",FACE,{"disambiguationData":[TD([[makeQuery(id+"F3.imprint","IMPRINT",EDGE,{"derivedFrom":makeQuery(id+"F2.imprint","IMPRINT",EDGE,{"derivedFrom":sQuery(id+"F2.wireOp",EDGE,"E93.MirrorC")})}),1.0]])]});
            var Q57;
            Q57=makeQuery(id+"F3.imprint","IMPRINT",FACE,{"disambiguationData":[TD([[makeQuery(id+"F3.imprint","IMPRINT",EDGE,{"derivedFrom":makeQuery(id+"F2.imprint","IMPRINT",EDGE,{"derivedFrom":sQuery(id+"F2.wireOp",EDGE,"E72.MirrorC")})}),-1.0]])]});
            var Q58;
            Q58=makeQuery(id+"F3.imprint","IMPRINT",FACE,{"disambiguationData":[TD([[makeQuery(id+"F3.imprint","IMPRINT",EDGE,{"derivedFrom":makeQuery(id+"F2.imprint","IMPRINT",EDGE,{"derivedFrom":sQuery(id+"F2.wireOp",EDGE,"E109.MirrorC")})}),1.0]])]});
            var Q59;
            Q59=makeQuery(id+"F3.imprint","IMPRINT",FACE,{"disambiguationData":[TD([[makeQuery(id+"F3.imprint","IMPRINT",EDGE,{"derivedFrom":makeQuery(id+"F2.imprint","IMPRINT",EDGE,{"derivedFrom":sQuery(id+"F2.wireOp",EDGE,"E86.MirrorC")})}),1.0]])]});
            var Q60;
            Q60=makeQuery(id+"F3.imprint","IMPRINT",FACE,{"disambiguationData":[TD([[makeQuery(id+"F3.imprint","IMPRINT",EDGE,{"derivedFrom":makeQuery(id+"F2.imprint","IMPRINT",EDGE,{"derivedFrom":sQuery(id+"F2.wireOp",EDGE,"E89.MirrorC")})}),1.0]])]});
            var Q61;
            Q61=makeQuery(id+"F3.imprint","IMPRINT",FACE,{"disambiguationData":[TD([[makeQuery(id+"F3.imprint","IMPRINT",EDGE,{"derivedFrom":makeQuery(id+"F2.imprint","IMPRINT",EDGE,{"derivedFrom":sQuery(id+"F2.wireOp",EDGE,"E108.MirrorC")})}),1.0]])]});
            var Q62;
            Q62=makeQuery(id+"F3.imprint","IMPRINT",FACE,{"disambiguationData":[TD([[makeQuery(id+"F3.imprint","IMPRINT",EDGE,{"derivedFrom":makeQuery(id+"F2.imprint","IMPRINT",EDGE,{"derivedFrom":sQuery(id+"F2.wireOp",EDGE,"E110.MirrorC")})}),1.0]])]});
            var Q63;
            Q63=makeQuery(id+"F3.imprint","IMPRINT",FACE,{"disambiguationData":[TD([[makeQuery(id+"F3.imprint","IMPRINT",EDGE,{"derivedFrom":makeQuery(id+"F2.imprint","IMPRINT",EDGE,{"derivedFrom":sQuery(id+"F2.wireOp",EDGE,"E69.MirrorC")})}),-1.0]])]});
            var Q64;
            Q64=makeQuery(id+"F3.imprint","IMPRINT",FACE,{"disambiguationData":[TD([[makeQuery(id+"F3.imprint","IMPRINT",EDGE,{"derivedFrom":makeQuery(id+"F2.imprint","IMPRINT",EDGE,{"derivedFrom":sQuery(id+"F2.wireOp",EDGE,"E102.MirrorC")})}),1.0]])]});
            var Q65;
            Q65=makeQuery(id+"F3.imprint","IMPRINT",FACE,{"disambiguationData":[TD([[makeQuery(id+"F3.imprint","IMPRINT",EDGE,{"derivedFrom":makeQuery(id+"F2.imprint","IMPRINT",EDGE,{"derivedFrom":sQuery(id+"F2.wireOp",EDGE,"E85.MirrorC")})}),1.0]])]});
            var Q66;
            Q66=makeQuery(id+"F3.imprint","IMPRINT",FACE,{"disambiguationData":[TD([[makeQuery(id+"F3.imprint","IMPRINT",EDGE,{"derivedFrom":makeQuery(id+"F2.imprint","IMPRINT",EDGE,{"derivedFrom":sQuery(id+"F2.wireOp",EDGE,"E71.MirrorC")})}),-1.0]])]});
            var Q67;
            Q67=makeQuery(id+"F3.imprint","IMPRINT",FACE,{"disambiguationData":[TD([[makeQuery(id+"F3.imprint","IMPRINT",EDGE,{"derivedFrom":makeQuery(id+"F2.imprint","IMPRINT",EDGE,{"derivedFrom":sQuery(id+"F2.wireOp",EDGE,"E106.MirrorC")})}),1.0]])]});
            var Q68;
            Q68=makeQuery(id+"F3.imprint","IMPRINT",FACE,{"disambiguationData":[TD([[makeQuery(id+"F3.imprint","IMPRINT",EDGE,{"derivedFrom":makeQuery(id+"F2.imprint","IMPRINT",EDGE,{"derivedFrom":sQuery(id+"F2.wireOp",EDGE,"E79.MirrorC")})}),1.0]])]});
            var Q69;
            Q69=makeQuery(id+"F3.imprint","IMPRINT",FACE,{"disambiguationData":[TD([[makeQuery(id+"F3.imprint","IMPRINT",EDGE,{"derivedFrom":makeQuery(id+"F2.imprint","IMPRINT",EDGE,{"derivedFrom":sQuery(id+"F2.wireOp",EDGE,"E81.MirrorC")})}),-1.0]])]});
            var Q70;
            Q70=makeQuery(id+"F3.imprint","IMPRINT",FACE,{"disambiguationData":[TD([[makeQuery(id+"F3.imprint","IMPRINT",EDGE,{"derivedFrom":makeQuery(id+"F2.imprint","IMPRINT",EDGE,{"derivedFrom":sQuery(id+"F2.wireOp",EDGE,"E96.MirrorC")})}),-1.0]])]});
            var Q71;
            Q71=makeQuery(id+"F3.imprint","IMPRINT",FACE,{"disambiguationData":[TD([[makeQuery(id+"F3.imprint","IMPRINT",EDGE,{"derivedFrom":makeQuery(id+"F2.imprint","IMPRINT",EDGE,{"derivedFrom":sQuery(id+"F2.wireOp",EDGE,"E78.MirrorC")})}),1.0]])]});
            var Q72;
            Q72=makeQuery(id+"F3.imprint","IMPRINT",FACE,{"disambiguationData":[TD([[makeQuery(id+"F3.imprint","IMPRINT",EDGE,{"derivedFrom":makeQuery(id+"F2.imprint","IMPRINT",EDGE,{"derivedFrom":sQuery(id+"F2.wireOp",EDGE,"E84.MirrorC")})}),-1.0]])]});
            var Q73;
            Q73=makeQuery(id+"F3.imprint","IMPRINT",FACE,{"disambiguationData":[TD([[makeQuery(id+"F3.imprint","IMPRINT",EDGE,{"derivedFrom":makeQuery(id+"F2.imprint","IMPRINT",EDGE,{"derivedFrom":sQuery(id+"F2.wireOp",EDGE,"E87.MirrorC")})}),-1.0]])]});
            var Q74;
            Q74=makeQuery(id+"F3.imprint","IMPRINT",FACE,{"disambiguationData":[TD([[makeQuery(id+"F3.imprint","IMPRINT",EDGE,{"derivedFrom":makeQuery(id+"F2.imprint","IMPRINT",EDGE,{"derivedFrom":sQuery(id+"F2.wireOp",EDGE,"E68")})}),1.0]])]});
            var Q75;
            Q75=makeQuery(id+"F3.imprint","IMPRINT",FACE,{"disambiguationData":[TD([[makeQuery(id+"F3.imprint","IMPRINT",EDGE,{"derivedFrom":makeQuery(id+"F2.imprint","IMPRINT",EDGE,{"derivedFrom":sQuery(id+"F2.wireOp",EDGE,"E94.MirrorC")})}),1.0]])]});
            var Q76;
            Q76=makeQuery(id+"F3.imprint","IMPRINT",FACE,{"disambiguationData":[TD([[makeQuery(id+"F3.imprint","IMPRINT",EDGE,{"derivedFrom":makeQuery(id+"F2.imprint","IMPRINT",EDGE,{"derivedFrom":sQuery(id+"F2.wireOp",EDGE,"E90.MirrorC")})}),1.0]])]});
            var Q77;
            Q77=makeQuery(id+"F3.imprint","IMPRINT",FACE,{"disambiguationData":[TD([[makeQuery(id+"F3.imprint","IMPRINT",EDGE,{"derivedFrom":makeQuery(id+"F2.imprint","IMPRINT",EDGE,{"derivedFrom":sQuery(id+"F2.wireOp",EDGE,"E98.MirrorC")})}),1.0]])]});
            var Q78;
            Q78=makeQuery(id+"F3.imprint","IMPRINT",FACE,{"disambiguationData":[TD([[makeQuery(id+"F3.imprint","IMPRINT",EDGE,{"derivedFrom":makeQuery(id+"F2.imprint","IMPRINT",EDGE,{"derivedFrom":sQuery(id+"F2.wireOp",EDGE,"E105.MirrorC")})}),1.0]])]});
            var Q79;
            Q79=makeQuery(id+"F3.imprint","IMPRINT",FACE,{"disambiguationData":[TD([[makeQuery(id+"F3.imprint","IMPRINT",EDGE,{"derivedFrom":makeQuery(id+"F2.imprint","IMPRINT",EDGE,{"derivedFrom":sQuery(id+"F2.wireOp",EDGE,"E70.MirrorC")})}),-1.0]])]});
            var Q80;
            Q80=makeQuery(id+"F3.imprint","IMPRINT",FACE,{"disambiguationData":[TD([[makeQuery(id+"F3.imprint","IMPRINT",EDGE,{"derivedFrom":makeQuery(id+"F2.imprint","IMPRINT",EDGE,{"derivedFrom":sQuery(id+"F2.wireOp",EDGE,"E83.MirrorC")})}),-1.0]])]});
            var Q81;
            Q81=makeQuery(id+"F2.imprint","IMPRINT",FACE,{"disambiguationData":[TD([[makeQuery(id+"F2.imprint","IMPRINT",EDGE,{"derivedFrom":sQuery(id+"F2.wireOp",EDGE,"E88.MirrorC")}),-1.0]])]});
            var Q82;
            Q82=makeQuery(id+"F2.imprint","IMPRINT",FACE,{"disambiguationData":[TD([[makeQuery(id+"F2.imprint","IMPRINT",EDGE,{"derivedFrom":sQuery(id+"F2.wireOp",EDGE,"E92.MirrorC")}),-1.0]])]});
            var Q83;
            Q83=makeQuery(id+"F2.imprint","IMPRINT",FACE,{"disambiguationData":[TD([[makeQuery(id+"F2.imprint","IMPRINT",EDGE,{"derivedFrom":sQuery(id+"F2.wireOp",EDGE,"E100.MirrorC")}),-1.0]])]});
            var Q84;
            Q84=makeQuery(id+"F2.imprint","IMPRINT",FACE,{"disambiguationData":[TD([[makeQuery(id+"F2.imprint","IMPRINT",EDGE,{"derivedFrom":sQuery(id+"F2.wireOp",EDGE,"E81.MirrorC")}),-1.0]])]});
            var Q85;
            Q85=makeQuery(id+"F2.imprint","IMPRINT",FACE,{"disambiguationData":[TD([[makeQuery(id+"F2.imprint","IMPRINT",EDGE,{"derivedFrom":sQuery(id+"F2.wireOp",EDGE,"E102.MirrorC")}),1.0]])]});
            var Q86;
            Q86=makeQuery(id+"F2.imprint","IMPRINT",FACE,{"disambiguationData":[TD([[makeQuery(id+"F2.imprint","IMPRINT",EDGE,{"derivedFrom":sQuery(id+"F2.wireOp",EDGE,"E94.MirrorC")}),1.0]])]});
            var Q87;
            Q87=makeQuery(id+"F2.imprint","IMPRINT",FACE,{"disambiguationData":[TD([[makeQuery(id+"F2.imprint","IMPRINT",EDGE,{"derivedFrom":sQuery(id+"F2.wireOp",EDGE,"E93.MirrorC")}),1.0]])]});
            var Q88;
            Q88=makeQuery(id+"F2.imprint","IMPRINT",FACE,{"disambiguationData":[TD([[makeQuery(id+"F2.imprint","IMPRINT",EDGE,{"derivedFrom":sQuery(id+"F2.wireOp",EDGE,"E82.MirrorC")}),-1.0]])]});
            var Q89;
            Q89=makeQuery(id+"F2.imprint","IMPRINT",FACE,{"disambiguationData":[TD([[makeQuery(id+"F2.imprint","IMPRINT",EDGE,{"derivedFrom":sQuery(id+"F2.wireOp",EDGE,"E104.MirrorC")}),1.0]])]});
            var Q90;
            Q90=makeQuery(id+"F2.imprint","IMPRINT",FACE,{"disambiguationData":[TD([[makeQuery(id+"F2.imprint","IMPRINT",EDGE,{"derivedFrom":sQuery(id+"F2.wireOp",EDGE,"E70.MirrorC")}),-1.0]])]});
            var Q91;
            Q91=makeQuery(id+"F2.imprint","IMPRINT",FACE,{"disambiguationData":[TD([[makeQuery(id+"F2.imprint","IMPRINT",EDGE,{"derivedFrom":sQuery(id+"F2.wireOp",EDGE,"E109.MirrorC")}),1.0]])]});
            var Q92;
            Q92=makeQuery(id+"F2.imprint","IMPRINT",FACE,{"disambiguationData":[TD([[makeQuery(id+"F2.imprint","IMPRINT",EDGE,{"derivedFrom":sQuery(id+"F2.wireOp",EDGE,"E99.MirrorC")}),-1.0]])]});
            var Q93;
            Q93=makeQuery(id+"F2.imprint","IMPRINT",FACE,{"disambiguationData":[TD([[makeQuery(id+"F2.imprint","IMPRINT",EDGE,{"derivedFrom":sQuery(id+"F2.wireOp",EDGE,"E69.MirrorC")}),-1.0]])]});
            var Q94;
            Q94=makeQuery(id+"F2.imprint","IMPRINT",FACE,{"disambiguationData":[TD([[makeQuery(id+"F2.imprint","IMPRINT",EDGE,{"derivedFrom":sQuery(id+"F2.wireOp",EDGE,"E72.MirrorC")}),-1.0]])]});
            var Q95;
            Q95=makeQuery(id+"F2.imprint","IMPRINT",FACE,{"disambiguationData":[TD([[makeQuery(id+"F2.imprint","IMPRINT",EDGE,{"derivedFrom":sQuery(id+"F2.wireOp",EDGE,"E71.MirrorC")}),-1.0]])]});
            var Q96;
            Q96=makeQuery(id+"F2.imprint","IMPRINT",FACE,{"disambiguationData":[TD([[makeQuery(id+"F2.imprint","IMPRINT",EDGE,{"derivedFrom":sQuery(id+"F2.wireOp",EDGE,"E85.MirrorC")}),1.0]])]});
            var Q97;
            Q97=makeQuery(id+"F2.imprint","IMPRINT",FACE,{"disambiguationData":[TD([[makeQuery(id+"F2.imprint","IMPRINT",EDGE,{"derivedFrom":sQuery(id+"F2.wireOp",EDGE,"E107.MirrorC")}),1.0]])]});
            var Q98;
            Q98=makeQuery(id+"F2.imprint","IMPRINT",FACE,{"disambiguationData":[TD([[makeQuery(id+"F2.imprint","IMPRINT",EDGE,{"derivedFrom":sQuery(id+"F2.wireOp",EDGE,"E87.MirrorC")}),-1.0]])]});
            var Q99;
            Q99=makeQuery(id+"F2.imprint","IMPRINT",FACE,{"disambiguationData":[TD([[makeQuery(id+"F2.imprint","IMPRINT",EDGE,{"derivedFrom":sQuery(id+"F2.wireOp",EDGE,"E96.MirrorC")}),-1.0]])]});
            var Q100;
            Q100=makeQuery(id+"F2.imprint","IMPRINT",FACE,{"disambiguationData":[TD([[makeQuery(id+"F2.imprint","IMPRINT",EDGE,{"derivedFrom":sQuery(id+"F2.wireOp",EDGE,"E78.MirrorC")}),1.0]])]});
            var Q101;
            Q101=makeQuery(id+"F2.imprint","IMPRINT",FACE,{"disambiguationData":[TD([[makeQuery(id+"F2.imprint","IMPRINT",EDGE,{"derivedFrom":sQuery(id+"F2.wireOp",EDGE,"E106.MirrorC")}),1.0]])]});
            var Q102;
            Q102=makeQuery(id+"F2.imprint","IMPRINT",FACE,{"disambiguationData":[TD([[makeQuery(id+"F2.imprint","IMPRINT",EDGE,{"derivedFrom":sQuery(id+"F2.wireOp",EDGE,"E98.MirrorC")}),1.0]])]});
            var Q103;
            Q103=makeQuery(id+"F2.imprint","IMPRINT",FACE,{"disambiguationData":[TD([[makeQuery(id+"F2.imprint","IMPRINT",EDGE,{"derivedFrom":sQuery(id+"F2.wireOp",EDGE,"E89.MirrorC")}),1.0]])]});
            var Q104;
            Q104=makeQuery(id+"F2.imprint","IMPRINT",FACE,{"disambiguationData":[TD([[makeQuery(id+"F2.imprint","IMPRINT",EDGE,{"derivedFrom":sQuery(id+"F2.wireOp",EDGE,"E103.MirrorC")}),1.0]])]});
            var Q105;
            Q105=makeQuery(id+"F2.imprint","IMPRINT",FACE,{"disambiguationData":[TD([[makeQuery(id+"F2.imprint","IMPRINT",EDGE,{"derivedFrom":sQuery(id+"F2.wireOp",EDGE,"E97.MirrorC")}),-1.0]])]});
            var Q106;
            Q106=makeQuery(id+"F2.imprint","IMPRINT",FACE,{"disambiguationData":[TD([[makeQuery(id+"F2.imprint","IMPRINT",EDGE,{"derivedFrom":sQuery(id+"F2.wireOp",EDGE,"E86.MirrorC")}),1.0]])]});
            var Q107;
            Q107=makeQuery(id+"F2.imprint","IMPRINT",FACE,{"disambiguationData":[TD([[makeQuery(id+"F2.imprint","IMPRINT",EDGE,{"derivedFrom":sQuery(id+"F2.wireOp",EDGE,"E95.MirrorC")}),1.0]])]});
            var Q108;
            Q108=makeQuery(id+"F2.imprint","IMPRINT",FACE,{"disambiguationData":[TD([[makeQuery(id+"F2.imprint","IMPRINT",EDGE,{"derivedFrom":sQuery(id+"F2.wireOp",EDGE,"E84.MirrorC")}),-1.0]])]});
            var Q109;
            Q109=makeQuery(id+"F2.imprint","IMPRINT",FACE,{"disambiguationData":[TD([[makeQuery(id+"F2.imprint","IMPRINT",EDGE,{"derivedFrom":sQuery(id+"F2.wireOp",EDGE,"E83.MirrorC")}),-1.0]])]});
            var Q110;
            Q110=makeQuery(id+"F2.imprint","IMPRINT",FACE,{"disambiguationData":[TD([[makeQuery(id+"F2.imprint","IMPRINT",EDGE,{"derivedFrom":sQuery(id+"F2.wireOp",EDGE,"E79.MirrorC")}),1.0]])]});
            var Q111;
            Q111=makeQuery(id+"F2.imprint","IMPRINT",FACE,{"disambiguationData":[TD([[makeQuery(id+"F2.imprint","IMPRINT",EDGE,{"derivedFrom":sQuery(id+"F2.wireOp",EDGE,"E108.MirrorC")}),1.0]])]});
            var Q112;
            Q112=makeQuery(id+"F2.imprint","IMPRINT",FACE,{"disambiguationData":[TD([[makeQuery(id+"F2.imprint","IMPRINT",EDGE,{"derivedFrom":sQuery(id+"F2.wireOp",EDGE,"E105.MirrorC")}),1.0]])]});
            var Q113;
            Q113=makeQuery(id+"F2.imprint","IMPRINT",FACE,{"disambiguationData":[TD([[makeQuery(id+"F2.imprint","IMPRINT",EDGE,{"derivedFrom":sQuery(id+"F2.wireOp",EDGE,"E68")}),1.0]])]});
            var Q114;
            Q114=makeQuery(id+"F2.imprint","IMPRINT",FACE,{"disambiguationData":[TD([[makeQuery(id+"F2.imprint","IMPRINT",EDGE,{"derivedFrom":sQuery(id+"F2.wireOp",EDGE,"E91.MirrorC")}),-1.0]])]});
            var Q115;
            Q115=makeQuery(id+"F2.imprint","IMPRINT",FACE,{"disambiguationData":[TD([[makeQuery(id+"F2.imprint","IMPRINT",EDGE,{"derivedFrom":sQuery(id+"F2.wireOp",EDGE,"E67")}),1.0]])]});
            var Q116;
            Q116=makeQuery(id+"F2.imprint","IMPRINT",FACE,{"disambiguationData":[TD([[makeQuery(id+"F2.imprint","IMPRINT",EDGE,{"derivedFrom":sQuery(id+"F2.wireOp",EDGE,"E74.MirrorC")}),1.0]])]});
            var Q117;
            Q117=makeQuery(id+"F2.imprint","IMPRINT",FACE,{"disambiguationData":[TD([[makeQuery(id+"F2.imprint","IMPRINT",EDGE,{"derivedFrom":sQuery(id+"F2.wireOp",EDGE,"E101.MirrorC")}),1.0]])]});
            var Q118;
            Q118=makeQuery(id+"F2.imprint","IMPRINT",FACE,{"disambiguationData":[TD([[makeQuery(id+"F2.imprint","IMPRINT",EDGE,{"derivedFrom":sQuery(id+"F2.wireOp",EDGE,"E90.MirrorC")}),1.0]])]});
            var Q119;
            Q119=makeQuery(id+"F2.imprint","IMPRINT",FACE,{"disambiguationData":[TD([[makeQuery(id+"F2.imprint","IMPRINT",EDGE,{"derivedFrom":sQuery(id+"F2.wireOp",EDGE,"E75.MirrorC")}),1.0]])]});
            var Q120;
            Q120=makeQuery(id+"F2.imprint","IMPRINT",FACE,{"disambiguationData":[TD([[makeQuery(id+"F2.imprint","IMPRINT",EDGE,{"derivedFrom":sQuery(id+"F2.wireOp",EDGE,"E110.MirrorC")}),1.0]])]});
            var Q121;
            Q121=makeQuery(id+"F3.imprint","IMPRINT",FACE,{"disambiguationData":[TD([[makeQuery(id+"F3.imprint","IMPRINT",EDGE,{"derivedFrom":makeQuery(id+"F2.imprint","IMPRINT",EDGE,{"derivedFrom":sQuery(id+"F2.wireOp",EDGE,"E66")})}),1.0]])]});
            var Q122;
            Q122=makeQuery(id+"F3.imprint","IMPRINT",FACE,{"disambiguationData":[TD([[makeQuery(id+"F3.imprint","IMPRINT",EDGE,{"derivedFrom":makeQuery(id+"F2.imprint","IMPRINT",EDGE,{"derivedFrom":sQuery(id+"F2.wireOp",EDGE,"E112.MirrorC")})}),1.0]])]});
            var Q123;
            Q123=makeQuery(id+"F3.imprint","IMPRINT",FACE,{"disambiguationData":[TD([[makeQuery(id+"F3.imprint","IMPRINT",EDGE,{"derivedFrom":makeQuery(id+"F2.imprint","IMPRINT",EDGE,{"derivedFrom":sQuery(id+"F2.wireOp",EDGE,"E114.MirrorC")})}),1.0]])]});
            var Q124;
            Q124=makeQuery(id+"F3.imprint","IMPRINT",FACE,{"disambiguationData":[TD([[makeQuery(id+"F3.imprint","IMPRINT",EDGE,{"derivedFrom":makeQuery(id+"F2.imprint","IMPRINT",EDGE,{"derivedFrom":sQuery(id+"F2.wireOp",EDGE,"E111.MirrorC")})}),1.0]])]});
            var Q125;
            Q125=makeQuery(id+"F3.imprint","IMPRINT",FACE,{"disambiguationData":[TD([[makeQuery(id+"F3.imprint","IMPRINT",EDGE,{"derivedFrom":makeQuery(id+"F2.imprint","IMPRINT",EDGE,{"derivedFrom":sQuery(id+"F2.wireOp",EDGE,"E113.MirrorC")})}),1.0]])]});
            var Q126;
            Q126=makeQuery(id+"F2.imprint","IMPRINT",FACE,{"disambiguationData":[TD([[makeQuery(id+"F2.imprint","IMPRINT",EDGE,{"derivedFrom":sQuery(id+"F2.wireOp",EDGE,"E66")}),1.0]])]});
            var Q127;
            Q127=makeQuery(id+"F2.imprint","IMPRINT",FACE,{"disambiguationData":[TD([[makeQuery(id+"F2.imprint","IMPRINT",EDGE,{"derivedFrom":sQuery(id+"F2.wireOp",EDGE,"E113.MirrorC")}),1.0]])]});
            var Q128;
            Q128=makeQuery(id+"F2.imprint","IMPRINT",FACE,{"disambiguationData":[TD([[makeQuery(id+"F2.imprint","IMPRINT",EDGE,{"derivedFrom":sQuery(id+"F2.wireOp",EDGE,"E114.MirrorC")}),1.0]])]});
            var Q129;
            Q129=makeQuery(id+"F2.imprint","IMPRINT",FACE,{"disambiguationData":[TD([[makeQuery(id+"F2.imprint","IMPRINT",EDGE,{"derivedFrom":sQuery(id+"F2.wireOp",EDGE,"E111.MirrorC")}),1.0]])]});
            var Q130;
            Q130=makeQuery(id+"F2.imprint","IMPRINT",FACE,{"disambiguationData":[TD([[makeQuery(id+"F2.imprint","IMPRINT",EDGE,{"derivedFrom":sQuery(id+"F2.wireOp",EDGE,"E112.MirrorC")}),1.0]])]});
            var Q131;
            Q131=makeQuery(id+"F3.imprint","IMPRINT",FACE,{"disambiguationData":[TD([[makeQuery(id+"F3.imprint","IMPRINT",EDGE,{"derivedFrom":makeQuery(id+"F2.imprint","IMPRINT",EDGE,{"derivedFrom":sQuery(id+"F2.wireOp",EDGE,"E44.MirrorCS")})}),-1.0]])]});
            var Q132;
            Q132=makeQuery(id+"F3.imprint","IMPRINT",FACE,{"disambiguationData":[TD([[makeQuery(id+"F3.imprint","IMPRINT",EDGE,{"derivedFrom":makeQuery(id+"F2.imprint","IMPRINT",EDGE,{"derivedFrom":sQuery(id+"F2.wireOp",EDGE,"30da4a9c-071b-46fc-a4fc-5d151489db350.MirrorCS")})}),1.0]])]});
            var Q133;
            Q133=makeQuery(id+"F3.imprint","IMPRINT",FACE,{"disambiguationData":[TD([[makeQuery(id+"F3.imprint","IMPRINT",EDGE,{"derivedFrom":makeQuery(id+"F2.imprint","IMPRINT",EDGE,{"derivedFrom":sQuery(id+"F2.wireOp",EDGE,"9e3958ab-8ce6-4a5b-9121-ec8d87c470c3.MirrorCS")})}),-1.0]])]});
            var Q134;
            Q134=makeQuery(id+"F3.imprint","IMPRINT",FACE,{"disambiguationData":[TD([[makeQuery(id+"F3.imprint","IMPRINT",EDGE,{"derivedFrom":makeQuery(id+"F2.imprint","IMPRINT",EDGE,{"derivedFrom":sQuery(id+"F2.wireOp",EDGE,"6145d215-bb94-4374-a2d7-bb32239ac7a20.MirrorCS")})}),-1.0]])]});
            var Q135;
            Q135=makeQuery(id+"F3.imprint","IMPRINT",FACE,{"disambiguationData":[TD([[makeQuery(id+"F3.imprint","IMPRINT",EDGE,{"derivedFrom":makeQuery(id+"F2.imprint","IMPRINT",EDGE,{"derivedFrom":sQuery(id+"F2.wireOp",EDGE,"7a27d959-d8b5-45a1-af6f-8aa5b613c5870.MirrorCS")})}),-1.0]])]});
            var Q136;
            Q136=makeQuery(id+"F3.imprint","IMPRINT",FACE,{"disambiguationData":[TD([[makeQuery(id+"F3.imprint","IMPRINT",EDGE,{"derivedFrom":makeQuery(id+"F2.imprint","IMPRINT",EDGE,{"derivedFrom":sQuery(id+"F2.wireOp",EDGE,"3a5b60a9-ad45-4b90-b108-ac97fdf74dc10.MirrorCS")})}),1.0]])]});
            var Q137;
            Q137=makeQuery(id+"F3.imprint","IMPRINT",FACE,{"disambiguationData":[TD([[makeQuery(id+"F3.imprint","IMPRINT",EDGE,{"derivedFrom":makeQuery(id+"F2.imprint","IMPRINT",EDGE,{"derivedFrom":sQuery(id+"F2.wireOp",EDGE,"E46.MirrorCS")})}),1.0]])]});
            var Q138;
            Q138=makeQuery(id+"F3.imprint","IMPRINT",FACE,{"disambiguationData":[TD([[makeQuery(id+"F3.imprint","IMPRINT",EDGE,{"derivedFrom":makeQuery(id+"F2.imprint","IMPRINT",EDGE,{"derivedFrom":sQuery(id+"F2.wireOp",EDGE,"22a68ee5-8228-4345-94e1-669d1aa4a0c80.MirrorCS")})}),1.0]])]});
            var Q139;
            Q139=makeQuery(id+"F3.imprint","IMPRINT",FACE,{"disambiguationData":[TD([[makeQuery(id+"F3.imprint","IMPRINT",EDGE,{"derivedFrom":makeQuery(id+"F2.imprint","IMPRINT",EDGE,{"derivedFrom":sQuery(id+"F2.wireOp",EDGE,"e6c6adc7-8afd-48a5-9f09-541ca7ef126d0.MirrorCS")})}),-1.0]])]});
            var Q140;
            Q140=makeQuery(id+"F3.imprint","IMPRINT",FACE,{"disambiguationData":[TD([[makeQuery(id+"F3.imprint","IMPRINT",EDGE,{"derivedFrom":makeQuery(id+"F2.imprint","IMPRINT",EDGE,{"derivedFrom":sQuery(id+"F2.wireOp",EDGE,"40216697-0143-415b-b75d-7f665f3563ae0.MirrorCS")})}),1.0]])]});
            var Q141;
            Q141=makeQuery(id+"F3.imprint","IMPRINT",FACE,{"disambiguationData":[TD([[makeQuery(id+"F3.imprint","IMPRINT",EDGE,{"derivedFrom":makeQuery(id+"F2.imprint","IMPRINT",EDGE,{"derivedFrom":sQuery(id+"F2.wireOp",EDGE,"6KtdoT9x-rWsy-FY7Z-YWYD-vtVlDtfl7iPq")})}),-1.0]])]});
            var Q142;
            Q142=makeQuery(id+"F2.imprint","IMPRINT",FACE,{"disambiguationData":[TD([[makeQuery(id+"F2.imprint","IMPRINT",EDGE,{"derivedFrom":sQuery(id+"F2.wireOp",EDGE,"9e3958ab-8ce6-4a5b-9121-ec8d87c470c3.MirrorCS")}),-1.0]])]});
            var Q143;
            Q143=makeQuery(id+"F2.imprint","IMPRINT",FACE,{"disambiguationData":[TD([[makeQuery(id+"F2.imprint","IMPRINT",EDGE,{"derivedFrom":sQuery(id+"F2.wireOp",EDGE,"6145d215-bb94-4374-a2d7-bb32239ac7a20.MirrorCS")}),-1.0]])]});
            var Q144;
            Q144=makeQuery(id+"F2.imprint","IMPRINT",FACE,{"disambiguationData":[TD([[makeQuery(id+"F2.imprint","IMPRINT",EDGE,{"derivedFrom":sQuery(id+"F2.wireOp",EDGE,"30da4a9c-071b-46fc-a4fc-5d151489db350.MirrorCS")}),1.0]])]});
            var Q145;
            Q145=makeQuery(id+"F2.imprint","IMPRINT",FACE,{"disambiguationData":[TD([[makeQuery(id+"F2.imprint","IMPRINT",EDGE,{"derivedFrom":sQuery(id+"F2.wireOp",EDGE,"E46.MirrorCS")}),1.0]])]});
            var Q146;
            Q146=makeQuery(id+"F2.imprint","IMPRINT",FACE,{"disambiguationData":[TD([[makeQuery(id+"F2.imprint","IMPRINT",EDGE,{"derivedFrom":sQuery(id+"F2.wireOp",EDGE,"40216697-0143-415b-b75d-7f665f3563ae0.MirrorCS")}),1.0]])]});
            var Q147;
            Q147=makeQuery(id+"F2.imprint","IMPRINT",FACE,{"disambiguationData":[TD([[makeQuery(id+"F2.imprint","IMPRINT",EDGE,{"derivedFrom":sQuery(id+"F2.wireOp",EDGE,"e6c6adc7-8afd-48a5-9f09-541ca7ef126d0.MirrorCS")}),-1.0]])]});
            var Q148;
            Q148=makeQuery(id+"F2.imprint","IMPRINT",FACE,{"disambiguationData":[TD([[makeQuery(id+"F2.imprint","IMPRINT",EDGE,{"derivedFrom":sQuery(id+"F2.wireOp",EDGE,"7a27d959-d8b5-45a1-af6f-8aa5b613c5870.MirrorCS")}),-1.0]])]});
            var Q149;
            Q149=makeQuery(id+"F2.imprint","IMPRINT",FACE,{"disambiguationData":[TD([[makeQuery(id+"F2.imprint","IMPRINT",EDGE,{"derivedFrom":sQuery(id+"F2.wireOp",EDGE,"22a68ee5-8228-4345-94e1-669d1aa4a0c80.MirrorCS")}),1.0]])]});
            var Q150;
            Q150=makeQuery(id+"F2.imprint","IMPRINT",FACE,{"disambiguationData":[TD([[makeQuery(id+"F2.imprint","IMPRINT",EDGE,{"derivedFrom":sQuery(id+"F2.wireOp",EDGE,"E44.MirrorCS")}),-1.0]])]});
            var Q151;
            Q151=makeQuery(id+"F2.imprint","IMPRINT",FACE,{"disambiguationData":[TD([[makeQuery(id+"F2.imprint","IMPRINT",EDGE,{"derivedFrom":sQuery(id+"F2.wireOp",EDGE,"3a5b60a9-ad45-4b90-b108-ac97fdf74dc10.MirrorCS")}),1.0]])]});
            var Q152;
            Q152=makeQuery(id+"F2.imprint","IMPRINT",FACE,{"disambiguationData":[TD([[makeQuery(id+"F2.imprint","IMPRINT",EDGE,{"derivedFrom":sQuery(id+"F2.wireOp",EDGE,"6KtdoT9x-rWsy-FY7Z-YWYD-vtVlDtfl7iPq")}),-1.0]])]});
            var Q153;
            Q153=makeQuery(id+"F2.imprint","IMPRINT",FACE,{"disambiguationData":[TD([[makeQuery(id+"F2.imprint","IMPRINT",EDGE,{"derivedFrom":sQuery(id+"F2.wireOp",EDGE,"E181.MirrorC")}),1.0]])]});
            var Q154;
            Q154=makeQuery(id+"F2.imprint","IMPRINT",FACE,{"disambiguationData":[TD([[makeQuery(id+"F2.imprint","IMPRINT",EDGE,{"derivedFrom":sQuery(id+"F2.wireOp",EDGE,"E154.MirrorC")}),1.0]])]});
            var Q155;
            Q155=makeQuery(id+"F2.imprint","IMPRINT",FACE,{"disambiguationData":[TD([[makeQuery(id+"F2.imprint","IMPRINT",EDGE,{"derivedFrom":sQuery(id+"F2.wireOp",EDGE,"E156.MirrorC")}),-1.0]])]});
            var Q156;
            Q156=makeQuery(id+"F2.imprint","IMPRINT",FACE,{"disambiguationData":[TD([[makeQuery(id+"F2.imprint","IMPRINT",EDGE,{"derivedFrom":sQuery(id+"F2.wireOp",EDGE,"E179.MirrorC")}),-1.0]])]});
            var Q157;
            Q157=makeQuery(id+"F2.imprint","IMPRINT",FACE,{"disambiguationData":[TD([[makeQuery(id+"F2.imprint","IMPRINT",EDGE,{"derivedFrom":sQuery(id+"F2.wireOp",EDGE,"E170.MirrorC")}),-1.0]])]});
            var Q158;
            Q158=makeQuery(id+"F2.imprint","IMPRINT",FACE,{"disambiguationData":[TD([[makeQuery(id+"F2.imprint","IMPRINT",EDGE,{"derivedFrom":sQuery(id+"F2.wireOp",EDGE,"E162.MirrorC")}),-1.0]])]});
            var Q159;
            Q159=makeQuery(id+"F2.imprint","IMPRINT",FACE,{"disambiguationData":[TD([[makeQuery(id+"F2.imprint","IMPRINT",EDGE,{"derivedFrom":sQuery(id+"F2.wireOp",EDGE,"E149.MirrorC")}),-1.0]])]});
            var Q160;
            Q160=makeQuery(id+"F2.imprint","IMPRINT",FACE,{"disambiguationData":[TD([[makeQuery(id+"F2.imprint","IMPRINT",EDGE,{"derivedFrom":sQuery(id+"F2.wireOp",EDGE,"E134.MirrorC")}),-1.0]])]});
            var Q161;
            Q161=makeQuery(id+"F2.imprint","IMPRINT",FACE,{"disambiguationData":[TD([[makeQuery(id+"F2.imprint","IMPRINT",EDGE,{"derivedFrom":sQuery(id+"F2.wireOp",EDGE,"E184.MirrorC")}),-1.0]])]});
            var Q162;
            Q162=makeQuery(id+"F2.imprint","IMPRINT",FACE,{"disambiguationData":[TD([[makeQuery(id+"F2.imprint","IMPRINT",EDGE,{"derivedFrom":sQuery(id+"F2.wireOp",EDGE,"E161.MirrorC")}),1.0]])]});
            var Q163;
            Q163=makeQuery(id+"F2.imprint","IMPRINT",FACE,{"disambiguationData":[TD([[makeQuery(id+"F2.imprint","IMPRINT",EDGE,{"derivedFrom":sQuery(id+"F2.wireOp",EDGE,"E143.MirrorC")}),-1.0]])]});
            var Q164;
            Q164=makeQuery(id+"F2.imprint","IMPRINT",FACE,{"disambiguationData":[TD([[makeQuery(id+"F2.imprint","IMPRINT",EDGE,{"derivedFrom":sQuery(id+"F2.wireOp",EDGE,"E172.MirrorC")}),1.0]])]});
            var Q165;
            Q165=makeQuery(id+"F2.imprint","IMPRINT",FACE,{"disambiguationData":[TD([[makeQuery(id+"F2.imprint","IMPRINT",EDGE,{"derivedFrom":sQuery(id+"F2.wireOp",EDGE,"E178.MirrorC")}),1.0]])]});
            var Q166;
            Q166=makeQuery(id+"F2.imprint","IMPRINT",FACE,{"disambiguationData":[TD([[makeQuery(id+"F2.imprint","IMPRINT",EDGE,{"derivedFrom":sQuery(id+"F2.wireOp",EDGE,"E159.MirrorC")}),1.0]])]});
            var Q167;
            Q167=makeQuery(id+"F2.imprint","IMPRINT",FACE,{"disambiguationData":[TD([[makeQuery(id+"F2.imprint","IMPRINT",EDGE,{"derivedFrom":sQuery(id+"F2.wireOp",EDGE,"E140.MirrorC")}),-1.0]])]});
            var Q168;
            Q168=makeQuery(id+"F2.imprint","IMPRINT",FACE,{"disambiguationData":[TD([[makeQuery(id+"F2.imprint","IMPRINT",EDGE,{"derivedFrom":sQuery(id+"F2.wireOp",EDGE,"E146.MirrorC")}),-1.0]])]});
            var Q169;
            Q169=makeQuery(id+"F2.imprint","IMPRINT",FACE,{"disambiguationData":[TD([[makeQuery(id+"F2.imprint","IMPRINT",EDGE,{"derivedFrom":sQuery(id+"F2.wireOp",EDGE,"E173.MirrorC")}),-1.0]])]});
            var Q170;
            Q170=makeQuery(id+"F2.imprint","IMPRINT",FACE,{"disambiguationData":[TD([[makeQuery(id+"F2.imprint","IMPRINT",EDGE,{"derivedFrom":sQuery(id+"F2.wireOp",EDGE,"E130.MirrorC")}),-1.0]])]});
            var Q171;
            Q171=makeQuery(id+"F2.imprint","IMPRINT",FACE,{"disambiguationData":[TD([[makeQuery(id+"F2.imprint","IMPRINT",EDGE,{"derivedFrom":sQuery(id+"F2.wireOp",EDGE,"E185.MirrorC")}),-1.0]])]});
            var Q172;
            Q172=makeQuery(id+"F2.imprint","IMPRINT",FACE,{"disambiguationData":[TD([[makeQuery(id+"F2.imprint","IMPRINT",EDGE,{"derivedFrom":sQuery(id+"F2.wireOp",EDGE,"E148.MirrorC")}),1.0]])]});
            var Q173;
            Q173=makeQuery(id+"F2.imprint","IMPRINT",FACE,{"disambiguationData":[TD([[makeQuery(id+"F2.imprint","IMPRINT",EDGE,{"derivedFrom":sQuery(id+"F2.wireOp",EDGE,"E141.MirrorC")}),-1.0]])]});
            var Q174;
            Q174=makeQuery(id+"F2.imprint","IMPRINT",FACE,{"disambiguationData":[TD([[makeQuery(id+"F2.imprint","IMPRINT",EDGE,{"derivedFrom":sQuery(id+"F2.wireOp",EDGE,"E175.MirrorC")}),-1.0]])]});
            var Q175;
            Q175=makeQuery(id+"F2.imprint","IMPRINT",FACE,{"disambiguationData":[TD([[makeQuery(id+"F2.imprint","IMPRINT",EDGE,{"derivedFrom":sQuery(id+"F2.wireOp",EDGE,"E183.MirrorC")}),1.0]])]});
            var Q176;
            Q176=makeQuery(id+"F2.imprint","IMPRINT",FACE,{"disambiguationData":[TD([[makeQuery(id+"F2.imprint","IMPRINT",EDGE,{"derivedFrom":sQuery(id+"F2.wireOp",EDGE,"E139.MirrorC")}),-1.0]])]});
            var Q177;
            Q177=makeQuery(id+"F2.imprint","IMPRINT",FACE,{"disambiguationData":[TD([[makeQuery(id+"F2.imprint","IMPRINT",EDGE,{"derivedFrom":sQuery(id+"F2.wireOp",EDGE,"E167.MirrorC")}),1.0]])]});
            var Q178;
            Q178=makeQuery(id+"F2.imprint","IMPRINT",FACE,{"disambiguationData":[TD([[makeQuery(id+"F2.imprint","IMPRINT",EDGE,{"derivedFrom":sQuery(id+"F2.wireOp",EDGE,"E137.MirrorC")}),-1.0]])]});
            var Q179;
            Q179=makeQuery(id+"F2.imprint","IMPRINT",FACE,{"disambiguationData":[TD([[makeQuery(id+"F2.imprint","IMPRINT",EDGE,{"derivedFrom":sQuery(id+"F2.wireOp",EDGE,"E176.MirrorC")}),-1.0]])]});
            var Q180;
            Q180=makeQuery(id+"F2.imprint","IMPRINT",FACE,{"disambiguationData":[TD([[makeQuery(id+"F2.imprint","IMPRINT",EDGE,{"derivedFrom":sQuery(id+"F2.wireOp",EDGE,"E158.MirrorC")}),-1.0]])]});
            var Q181;
            Q181=makeQuery(id+"F2.imprint","IMPRINT",FACE,{"disambiguationData":[TD([[makeQuery(id+"F2.imprint","IMPRINT",EDGE,{"derivedFrom":sQuery(id+"F2.wireOp",EDGE,"E163.MirrorC")}),-1.0]])]});
            var Q182;
            Q182=makeQuery(id+"F2.imprint","IMPRINT",FACE,{"disambiguationData":[TD([[makeQuery(id+"F2.imprint","IMPRINT",EDGE,{"derivedFrom":sQuery(id+"F2.wireOp",EDGE,"E182.MirrorC")}),-1.0]])]});
            var Q183;
            Q183=makeQuery(id+"F2.imprint","IMPRINT",FACE,{"disambiguationData":[TD([[makeQuery(id+"F2.imprint","IMPRINT",EDGE,{"derivedFrom":sQuery(id+"F2.wireOp",EDGE,"E168.MirrorC")}),-1.0]])]});
            var Q184;
            Q184=makeQuery(id+"F2.imprint","IMPRINT",FACE,{"disambiguationData":[TD([[makeQuery(id+"F2.imprint","IMPRINT",EDGE,{"derivedFrom":sQuery(id+"F2.wireOp",EDGE,"E165.MirrorC")}),1.0]])]});
            var Q185;
            Q185=makeQuery(id+"F2.imprint","IMPRINT",FACE,{"disambiguationData":[TD([[makeQuery(id+"F2.imprint","IMPRINT",EDGE,{"derivedFrom":sQuery(id+"F2.wireOp",EDGE,"E129.MirrorC")}),-1.0]])]});
            var Q186;
            Q186=makeQuery(id+"F2.imprint","IMPRINT",FACE,{"disambiguationData":[TD([[makeQuery(id+"F2.imprint","IMPRINT",EDGE,{"derivedFrom":sQuery(id+"F2.wireOp",EDGE,"E150.MirrorC")}),-1.0]])]});
            var Q187;
            Q187=makeQuery(id+"F2.imprint","IMPRINT",FACE,{"disambiguationData":[TD([[makeQuery(id+"F2.imprint","IMPRINT",EDGE,{"derivedFrom":sQuery(id+"F2.wireOp",EDGE,"E142.MirrorC")}),-1.0]])]});
            var Q188;
            Q188=makeQuery(id+"F2.imprint","IMPRINT",FACE,{"disambiguationData":[TD([[makeQuery(id+"F2.imprint","IMPRINT",EDGE,{"derivedFrom":sQuery(id+"F2.wireOp",EDGE,"E166.MirrorC")}),-1.0]])]});
            var Q189;
            Q189=makeQuery(id+"F2.imprint","IMPRINT",FACE,{"disambiguationData":[TD([[makeQuery(id+"F2.imprint","IMPRINT",EDGE,{"derivedFrom":sQuery(id+"F2.wireOp",EDGE,"E160.MirrorC")}),1.0]])]});
            var Q190;
            Q190=makeQuery(id+"F2.imprint","IMPRINT",FACE,{"disambiguationData":[TD([[makeQuery(id+"F2.imprint","IMPRINT",EDGE,{"derivedFrom":sQuery(id+"F2.wireOp",EDGE,"E180.MirrorC")}),1.0]])]});
            var Q191;
            Q191=makeQuery(id+"F2.imprint","IMPRINT",FACE,{"disambiguationData":[TD([[makeQuery(id+"F2.imprint","IMPRINT",EDGE,{"derivedFrom":sQuery(id+"F2.wireOp",EDGE,"E177.MirrorC")}),-1.0]])]});
            var Q192;
            Q192=makeQuery(id+"F2.imprint","IMPRINT",FACE,{"disambiguationData":[TD([[makeQuery(id+"F2.imprint","IMPRINT",EDGE,{"derivedFrom":sQuery(id+"F2.wireOp",EDGE,"E145.MirrorC")}),-1.0]])]});
            var Q193;
            Q193=makeQuery(id+"F2.imprint","IMPRINT",FACE,{"disambiguationData":[TD([[makeQuery(id+"F2.imprint","IMPRINT",EDGE,{"derivedFrom":sQuery(id+"F2.wireOp",EDGE,"E118.MirrorC")}),-1.0]])]});
            var Q194;
            Q194=makeQuery(id+"F2.imprint","IMPRINT",FACE,{"disambiguationData":[TD([[makeQuery(id+"F2.imprint","IMPRINT",EDGE,{"derivedFrom":sQuery(id+"F2.wireOp",EDGE,"E131.MirrorC")}),-1.0]])]});
            var Q195;
            Q195=makeQuery(id+"F2.imprint","IMPRINT",FACE,{"disambiguationData":[TD([[makeQuery(id+"F2.imprint","IMPRINT",EDGE,{"derivedFrom":sQuery(id+"F2.wireOp",EDGE,"E138.MirrorC")}),-1.0]])]});
            var Q196;
            Q196=makeQuery(id+"F2.imprint","IMPRINT",FACE,{"disambiguationData":[TD([[makeQuery(id+"F2.imprint","IMPRINT",EDGE,{"derivedFrom":sQuery(id+"F2.wireOp",EDGE,"E147.MirrorC")}),1.0]])]});
            var Q197;
            Q197=makeQuery(id+"F2.imprint","IMPRINT",FACE,{"disambiguationData":[TD([[makeQuery(id+"F2.imprint","IMPRINT",EDGE,{"derivedFrom":sQuery(id+"F2.wireOp",EDGE,"E169.MirrorC")}),1.0]])]});
            var Q198;
            Q198=makeQuery(id+"F2.imprint","IMPRINT",FACE,{"disambiguationData":[TD([[makeQuery(id+"F2.imprint","IMPRINT",EDGE,{"derivedFrom":sQuery(id+"F2.wireOp",EDGE,"E174.MirrorC")}),1.0]])]});
            var Q199;
            Q199=makeQuery(id+"F2.imprint","IMPRINT",FACE,{"disambiguationData":[TD([[makeQuery(id+"F2.imprint","IMPRINT",EDGE,{"derivedFrom":sQuery(id+"F2.wireOp",EDGE,"E126.MirrorC")}),-1.0]])]});
            var Q200;
            Q200=makeQuery(id+"F2.imprint","IMPRINT",FACE,{"disambiguationData":[TD([[makeQuery(id+"F2.imprint","IMPRINT",EDGE,{"derivedFrom":sQuery(id+"F2.wireOp",EDGE,"E164.MirrorC")}),1.0]])]});
            var Q201;
            Q201=makeQuery(id+"F2.imprint","IMPRINT",FACE,{"disambiguationData":[TD([[makeQuery(id+"F2.imprint","IMPRINT",EDGE,{"derivedFrom":sQuery(id+"F2.wireOp",EDGE,"E171.MirrorC")}),-1.0]])]});
            var Q202;
            Q202=makeQuery(id+"F2.imprint","IMPRINT",FACE,{"disambiguationData":[TD([[makeQuery(id+"F2.imprint","IMPRINT",EDGE,{"derivedFrom":sQuery(id+"F2.wireOp",EDGE,"E125.MirrorC")}),-1.0]])]});
            var Q203;
            Q203=makeQuery(id+"F2.imprint","IMPRINT",FACE,{"disambiguationData":[TD([[makeQuery(id+"F2.imprint","IMPRINT",EDGE,{"derivedFrom":sQuery(id+"F2.wireOp",EDGE,"E157.MirrorC")}),1.0]])]});
            var Q204;
            Q204=makeQuery(id+"F2.imprint","IMPRINT",FACE,{"disambiguationData":[TD([[makeQuery(id+"F2.imprint","IMPRINT",EDGE,{"derivedFrom":sQuery(id+"F2.wireOp",EDGE,"E151.MirrorC")}),1.0]])]});
            var Q205;
            Q205=makeQuery(id+"F2.imprint","IMPRINT",FACE,{"disambiguationData":[TD([[makeQuery(id+"F2.imprint","IMPRINT",EDGE,{"derivedFrom":sQuery(id+"F2.wireOp",EDGE,"E123.MirrorC")}),-1.0]])]});
            var Q206;
            Q206=makeQuery(id+"F2.imprint","IMPRINT",FACE,{"disambiguationData":[TD([[makeQuery(id+"F2.imprint","IMPRINT",EDGE,{"derivedFrom":sQuery(id+"F2.wireOp",EDGE,"E153.MirrorC")}),1.0]])]});
            var Q207;
            Q207=makeQuery(id+"F2.imprint","IMPRINT",FACE,{"disambiguationData":[TD([[makeQuery(id+"F2.imprint","IMPRINT",EDGE,{"derivedFrom":sQuery(id+"F2.wireOp",EDGE,"E155.MirrorC")}),1.0]])]});
            var Q208;
            Q208=makeQuery(id+"F2.imprint","IMPRINT",FACE,{"disambiguationData":[TD([[makeQuery(id+"F2.imprint","IMPRINT",EDGE,{"derivedFrom":sQuery(id+"F2.wireOp",EDGE,"E152.MirrorC")}),-1.0]])]});
            var Q209;
            Q209=makeQuery(id+"F2.imprint","IMPRINT",FACE,{"disambiguationData":[TD([[makeQuery(id+"F2.imprint","IMPRINT",EDGE,{"derivedFrom":sQuery(id+"F2.wireOp",EDGE,"E132.MirrorC")}),-1.0]])]});
            var Q210;
            Q210=makeQuery(id+"F2.imprint","IMPRINT",FACE,{"disambiguationData":[TD([[makeQuery(id+"F2.imprint","IMPRINT",EDGE,{"derivedFrom":sQuery(id+"F2.wireOp",EDGE,"E128.MirrorC")}),-1.0]])]});
            var Q211;
            Q211=makeQuery(id+"F2.imprint","IMPRINT",FACE,{"disambiguationData":[TD([[makeQuery(id+"F2.imprint","IMPRINT",EDGE,{"derivedFrom":sQuery(id+"F2.wireOp",EDGE,"E121.MirrorC")}),-1.0]])]});
            var Q212;
            Q212=makeQuery(id+"F2.imprint","IMPRINT",FACE,{"disambiguationData":[TD([[makeQuery(id+"F2.imprint","IMPRINT",EDGE,{"derivedFrom":sQuery(id+"F2.wireOp",EDGE,"E119.MirrorC")}),-1.0]])]});
            var Q213;
            Q213=makeQuery(id+"F3.imprint","IMPRINT",FACE,{"disambiguationData":[TD([[makeQuery(id+"F3.imprint","IMPRINT",EDGE,{"derivedFrom":makeQuery(id+"F2.imprint","IMPRINT",EDGE,{"derivedFrom":sQuery(id+"F2.wireOp",EDGE,"E140.MirrorC")})}),-1.0]])]});
            var Q214;
            Q214=makeQuery(id+"F3.imprint","IMPRINT",FACE,{"disambiguationData":[TD([[makeQuery(id+"F3.imprint","IMPRINT",EDGE,{"derivedFrom":makeQuery(id+"F2.imprint","IMPRINT",EDGE,{"derivedFrom":sQuery(id+"F2.wireOp",EDGE,"E141.MirrorC")})}),-1.0]])]});
            var Q215;
            Q215=makeQuery(id+"F3.imprint","IMPRINT",FACE,{"disambiguationData":[TD([[makeQuery(id+"F3.imprint","IMPRINT",EDGE,{"derivedFrom":makeQuery(id+"F2.imprint","IMPRINT",EDGE,{"derivedFrom":sQuery(id+"F2.wireOp",EDGE,"E142.MirrorC")})}),-1.0]])]});
            var Q216;
            Q216=makeQuery(id+"F3.imprint","IMPRINT",FACE,{"disambiguationData":[TD([[makeQuery(id+"F3.imprint","IMPRINT",EDGE,{"derivedFrom":makeQuery(id+"F2.imprint","IMPRINT",EDGE,{"derivedFrom":sQuery(id+"F2.wireOp",EDGE,"E143.MirrorC")})}),-1.0]])]});
            var Q217;
            Q217=makeQuery(id+"F3.imprint","IMPRINT",FACE,{"disambiguationData":[TD([[makeQuery(id+"F3.imprint","IMPRINT",EDGE,{"derivedFrom":makeQuery(id+"F2.imprint","IMPRINT",EDGE,{"derivedFrom":sQuery(id+"F2.wireOp",EDGE,"E145.MirrorC")})}),-1.0]])]});
            var Q218;
            Q218=makeQuery(id+"F3.imprint","IMPRINT",FACE,{"disambiguationData":[TD([[makeQuery(id+"F3.imprint","IMPRINT",EDGE,{"derivedFrom":makeQuery(id+"F2.imprint","IMPRINT",EDGE,{"derivedFrom":sQuery(id+"F2.wireOp",EDGE,"E146.MirrorC")})}),-1.0]])]});
            var Q219;
            Q219=makeQuery(id+"F3.imprint","IMPRINT",FACE,{"disambiguationData":[TD([[makeQuery(id+"F3.imprint","IMPRINT",EDGE,{"derivedFrom":makeQuery(id+"F2.imprint","IMPRINT",EDGE,{"derivedFrom":sQuery(id+"F2.wireOp",EDGE,"E147.MirrorC")})}),1.0]])]});
            var Q220;
            Q220=makeQuery(id+"F3.imprint","IMPRINT",FACE,{"disambiguationData":[TD([[makeQuery(id+"F3.imprint","IMPRINT",EDGE,{"derivedFrom":makeQuery(id+"F2.imprint","IMPRINT",EDGE,{"derivedFrom":sQuery(id+"F2.wireOp",EDGE,"E148.MirrorC")})}),1.0]])]});
            var Q221;
            Q221=makeQuery(id+"F3.imprint","IMPRINT",FACE,{"disambiguationData":[TD([[makeQuery(id+"F3.imprint","IMPRINT",EDGE,{"derivedFrom":makeQuery(id+"F2.imprint","IMPRINT",EDGE,{"derivedFrom":sQuery(id+"F2.wireOp",EDGE,"E149.MirrorC")})}),-1.0]])]});
            var Q222;
            Q222=makeQuery(id+"F3.imprint","IMPRINT",FACE,{"disambiguationData":[TD([[makeQuery(id+"F3.imprint","IMPRINT",EDGE,{"derivedFrom":makeQuery(id+"F2.imprint","IMPRINT",EDGE,{"derivedFrom":sQuery(id+"F2.wireOp",EDGE,"E150.MirrorC")})}),-1.0]])]});
            var Q223;
            Q223=makeQuery(id+"F3.imprint","IMPRINT",FACE,{"disambiguationData":[TD([[makeQuery(id+"F3.imprint","IMPRINT",EDGE,{"derivedFrom":makeQuery(id+"F2.imprint","IMPRINT",EDGE,{"derivedFrom":sQuery(id+"F2.wireOp",EDGE,"E151.MirrorC")})}),1.0]])]});
            var Q224;
            Q224=makeQuery(id+"F3.imprint","IMPRINT",FACE,{"disambiguationData":[TD([[makeQuery(id+"F3.imprint","IMPRINT",EDGE,{"derivedFrom":makeQuery(id+"F2.imprint","IMPRINT",EDGE,{"derivedFrom":sQuery(id+"F2.wireOp",EDGE,"E152.MirrorC")})}),-1.0]])]});
            var Q225;
            Q225=makeQuery(id+"F3.imprint","IMPRINT",FACE,{"disambiguationData":[TD([[makeQuery(id+"F3.imprint","IMPRINT",EDGE,{"derivedFrom":makeQuery(id+"F2.imprint","IMPRINT",EDGE,{"derivedFrom":sQuery(id+"F2.wireOp",EDGE,"E153.MirrorC")})}),1.0]])]});
            var Q226;
            Q226=makeQuery(id+"F3.imprint","IMPRINT",FACE,{"disambiguationData":[TD([[makeQuery(id+"F3.imprint","IMPRINT",EDGE,{"derivedFrom":makeQuery(id+"F2.imprint","IMPRINT",EDGE,{"derivedFrom":sQuery(id+"F2.wireOp",EDGE,"E154.MirrorC")})}),1.0]])]});
            var Q227;
            Q227=makeQuery(id+"F3.imprint","IMPRINT",FACE,{"disambiguationData":[TD([[makeQuery(id+"F3.imprint","IMPRINT",EDGE,{"derivedFrom":makeQuery(id+"F2.imprint","IMPRINT",EDGE,{"derivedFrom":sQuery(id+"F2.wireOp",EDGE,"E155.MirrorC")})}),1.0]])]});
            var Q228;
            Q228=makeQuery(id+"F3.imprint","IMPRINT",FACE,{"disambiguationData":[TD([[makeQuery(id+"F3.imprint","IMPRINT",EDGE,{"derivedFrom":makeQuery(id+"F2.imprint","IMPRINT",EDGE,{"derivedFrom":sQuery(id+"F2.wireOp",EDGE,"E156.MirrorC")})}),-1.0]])]});
            var Q229;
            Q229=makeQuery(id+"F3.imprint","IMPRINT",FACE,{"disambiguationData":[TD([[makeQuery(id+"F3.imprint","IMPRINT",EDGE,{"derivedFrom":makeQuery(id+"F2.imprint","IMPRINT",EDGE,{"derivedFrom":sQuery(id+"F2.wireOp",EDGE,"E157.MirrorC")})}),1.0]])]});
            var Q230;
            Q230=makeQuery(id+"F3.imprint","IMPRINT",FACE,{"disambiguationData":[TD([[makeQuery(id+"F3.imprint","IMPRINT",EDGE,{"derivedFrom":makeQuery(id+"F2.imprint","IMPRINT",EDGE,{"derivedFrom":sQuery(id+"F2.wireOp",EDGE,"E158.MirrorC")})}),-1.0]])]});
            var Q231;
            Q231=makeQuery(id+"F3.imprint","IMPRINT",FACE,{"disambiguationData":[TD([[makeQuery(id+"F3.imprint","IMPRINT",EDGE,{"derivedFrom":makeQuery(id+"F2.imprint","IMPRINT",EDGE,{"derivedFrom":sQuery(id+"F2.wireOp",EDGE,"E159.MirrorC")})}),1.0]])]});
            var Q232;
            Q232=makeQuery(id+"F3.imprint","IMPRINT",FACE,{"disambiguationData":[TD([[makeQuery(id+"F3.imprint","IMPRINT",EDGE,{"derivedFrom":makeQuery(id+"F2.imprint","IMPRINT",EDGE,{"derivedFrom":sQuery(id+"F2.wireOp",EDGE,"E160.MirrorC")})}),1.0]])]});
            var Q233;
            Q233=makeQuery(id+"F3.imprint","IMPRINT",FACE,{"disambiguationData":[TD([[makeQuery(id+"F3.imprint","IMPRINT",EDGE,{"derivedFrom":makeQuery(id+"F2.imprint","IMPRINT",EDGE,{"derivedFrom":sQuery(id+"F2.wireOp",EDGE,"E161.MirrorC")})}),1.0]])]});
            var Q234;
            Q234=makeQuery(id+"F3.imprint","IMPRINT",FACE,{"disambiguationData":[TD([[makeQuery(id+"F3.imprint","IMPRINT",EDGE,{"derivedFrom":makeQuery(id+"F2.imprint","IMPRINT",EDGE,{"derivedFrom":sQuery(id+"F2.wireOp",EDGE,"E162.MirrorC")})}),-1.0]])]});
            var Q235;
            Q235=makeQuery(id+"F3.imprint","IMPRINT",FACE,{"disambiguationData":[TD([[makeQuery(id+"F3.imprint","IMPRINT",EDGE,{"derivedFrom":makeQuery(id+"F2.imprint","IMPRINT",EDGE,{"derivedFrom":sQuery(id+"F2.wireOp",EDGE,"E163.MirrorC")})}),-1.0]])]});
            var Q236;
            Q236=makeQuery(id+"F3.imprint","IMPRINT",FACE,{"disambiguationData":[TD([[makeQuery(id+"F3.imprint","IMPRINT",EDGE,{"derivedFrom":makeQuery(id+"F2.imprint","IMPRINT",EDGE,{"derivedFrom":sQuery(id+"F2.wireOp",EDGE,"E164.MirrorC")})}),1.0]])]});
            var Q237;
            Q237=makeQuery(id+"F3.imprint","IMPRINT",FACE,{"disambiguationData":[TD([[makeQuery(id+"F3.imprint","IMPRINT",EDGE,{"derivedFrom":makeQuery(id+"F2.imprint","IMPRINT",EDGE,{"derivedFrom":sQuery(id+"F2.wireOp",EDGE,"E177.MirrorC")})}),-1.0]])]});
            var Q238;
            Q238=makeQuery(id+"F3.imprint","IMPRINT",FACE,{"disambiguationData":[TD([[makeQuery(id+"F3.imprint","IMPRINT",EDGE,{"derivedFrom":makeQuery(id+"F2.imprint","IMPRINT",EDGE,{"derivedFrom":sQuery(id+"F2.wireOp",EDGE,"E178.MirrorC")})}),1.0]])]});
            var Q239;
            Q239=makeQuery(id+"F3.imprint","IMPRINT",FACE,{"disambiguationData":[TD([[makeQuery(id+"F3.imprint","IMPRINT",EDGE,{"derivedFrom":makeQuery(id+"F2.imprint","IMPRINT",EDGE,{"derivedFrom":sQuery(id+"F2.wireOp",EDGE,"E179.MirrorC")})}),-1.0]])]});
            var Q240;
            Q240=makeQuery(id+"F3.imprint","IMPRINT",FACE,{"disambiguationData":[TD([[makeQuery(id+"F3.imprint","IMPRINT",EDGE,{"derivedFrom":makeQuery(id+"F2.imprint","IMPRINT",EDGE,{"derivedFrom":sQuery(id+"F2.wireOp",EDGE,"E180.MirrorC")})}),1.0]])]});
            var Q241;
            Q241=makeQuery(id+"F3.imprint","IMPRINT",FACE,{"disambiguationData":[TD([[makeQuery(id+"F3.imprint","IMPRINT",EDGE,{"derivedFrom":makeQuery(id+"F2.imprint","IMPRINT",EDGE,{"derivedFrom":sQuery(id+"F2.wireOp",EDGE,"E181.MirrorC")})}),1.0]])]});
            var Q242;
            Q242=makeQuery(id+"F3.imprint","IMPRINT",FACE,{"disambiguationData":[TD([[makeQuery(id+"F3.imprint","IMPRINT",EDGE,{"derivedFrom":makeQuery(id+"F2.imprint","IMPRINT",EDGE,{"derivedFrom":sQuery(id+"F2.wireOp",EDGE,"E182.MirrorC")})}),-1.0]])]});
            var Q243;
            Q243=makeQuery(id+"F3.imprint","IMPRINT",FACE,{"disambiguationData":[TD([[makeQuery(id+"F3.imprint","IMPRINT",EDGE,{"derivedFrom":makeQuery(id+"F2.imprint","IMPRINT",EDGE,{"derivedFrom":sQuery(id+"F2.wireOp",EDGE,"E185.MirrorC")})}),-1.0]])]});
            var Q244;
            Q244=makeQuery(id+"F3.imprint","IMPRINT",FACE,{"disambiguationData":[TD([[makeQuery(id+"F3.imprint","IMPRINT",EDGE,{"derivedFrom":makeQuery(id+"F2.imprint","IMPRINT",EDGE,{"derivedFrom":sQuery(id+"F2.wireOp",EDGE,"E184.MirrorC")})}),-1.0]])]});
            var Q245;
            Q245=makeQuery(id+"F3.imprint","IMPRINT",FACE,{"disambiguationData":[TD([[makeQuery(id+"F3.imprint","IMPRINT",EDGE,{"derivedFrom":makeQuery(id+"F2.imprint","IMPRINT",EDGE,{"derivedFrom":sQuery(id+"F2.wireOp",EDGE,"E183.MirrorC")})}),1.0]])]});
            var Q246;
            Q246=makeQuery(id+"F3.imprint","IMPRINT",FACE,{"disambiguationData":[TD([[makeQuery(id+"F3.imprint","IMPRINT",EDGE,{"derivedFrom":makeQuery(id+"F2.imprint","IMPRINT",EDGE,{"derivedFrom":sQuery(id+"F2.wireOp",EDGE,"E176.MirrorC")})}),-1.0]])]});
            var Q247;
            Q247=makeQuery(id+"F3.imprint","IMPRINT",FACE,{"disambiguationData":[TD([[makeQuery(id+"F3.imprint","IMPRINT",EDGE,{"derivedFrom":makeQuery(id+"F2.imprint","IMPRINT",EDGE,{"derivedFrom":sQuery(id+"F2.wireOp",EDGE,"E175.MirrorC")})}),-1.0]])]});
            var Q248;
            Q248=makeQuery(id+"F3.imprint","IMPRINT",FACE,{"disambiguationData":[TD([[makeQuery(id+"F3.imprint","IMPRINT",EDGE,{"derivedFrom":makeQuery(id+"F2.imprint","IMPRINT",EDGE,{"derivedFrom":sQuery(id+"F2.wireOp",EDGE,"E174.MirrorC")})}),1.0]])]});
            var Q249;
            Q249=makeQuery(id+"F3.imprint","IMPRINT",FACE,{"disambiguationData":[TD([[makeQuery(id+"F3.imprint","IMPRINT",EDGE,{"derivedFrom":makeQuery(id+"F2.imprint","IMPRINT",EDGE,{"derivedFrom":sQuery(id+"F2.wireOp",EDGE,"E173.MirrorC")})}),-1.0]])]});
            var Q250;
            Q250=makeQuery(id+"F3.imprint","IMPRINT",FACE,{"disambiguationData":[TD([[makeQuery(id+"F3.imprint","IMPRINT",EDGE,{"derivedFrom":makeQuery(id+"F2.imprint","IMPRINT",EDGE,{"derivedFrom":sQuery(id+"F2.wireOp",EDGE,"E172.MirrorC")})}),1.0]])]});
            var Q251;
            Q251=makeQuery(id+"F3.imprint","IMPRINT",FACE,{"disambiguationData":[TD([[makeQuery(id+"F3.imprint","IMPRINT",EDGE,{"derivedFrom":makeQuery(id+"F2.imprint","IMPRINT",EDGE,{"derivedFrom":sQuery(id+"F2.wireOp",EDGE,"E171.MirrorC")})}),-1.0]])]});
            var Q252;
            Q252=makeQuery(id+"F3.imprint","IMPRINT",FACE,{"disambiguationData":[TD([[makeQuery(id+"F3.imprint","IMPRINT",EDGE,{"derivedFrom":makeQuery(id+"F2.imprint","IMPRINT",EDGE,{"derivedFrom":sQuery(id+"F2.wireOp",EDGE,"E170.MirrorC")})}),-1.0]])]});
            var Q253;
            Q253=makeQuery(id+"F3.imprint","IMPRINT",FACE,{"disambiguationData":[TD([[makeQuery(id+"F3.imprint","IMPRINT",EDGE,{"derivedFrom":makeQuery(id+"F2.imprint","IMPRINT",EDGE,{"derivedFrom":sQuery(id+"F2.wireOp",EDGE,"E169.MirrorC")})}),1.0]])]});
            var Q254;
            Q254=makeQuery(id+"F3.imprint","IMPRINT",FACE,{"disambiguationData":[TD([[makeQuery(id+"F3.imprint","IMPRINT",EDGE,{"derivedFrom":makeQuery(id+"F2.imprint","IMPRINT",EDGE,{"derivedFrom":sQuery(id+"F2.wireOp",EDGE,"E168.MirrorC")})}),-1.0]])]});
            var Q255;
            Q255=makeQuery(id+"F3.imprint","IMPRINT",FACE,{"disambiguationData":[TD([[makeQuery(id+"F3.imprint","IMPRINT",EDGE,{"derivedFrom":makeQuery(id+"F2.imprint","IMPRINT",EDGE,{"derivedFrom":sQuery(id+"F2.wireOp",EDGE,"E167.MirrorC")})}),1.0]])]});
            var Q256;
            Q256=makeQuery(id+"F3.imprint","IMPRINT",FACE,{"disambiguationData":[TD([[makeQuery(id+"F3.imprint","IMPRINT",EDGE,{"derivedFrom":makeQuery(id+"F2.imprint","IMPRINT",EDGE,{"derivedFrom":sQuery(id+"F2.wireOp",EDGE,"E166.MirrorC")})}),-1.0]])]});
            var Q257;
            Q257=makeQuery(id+"F3.imprint","IMPRINT",FACE,{"disambiguationData":[TD([[makeQuery(id+"F3.imprint","IMPRINT",EDGE,{"derivedFrom":makeQuery(id+"F2.imprint","IMPRINT",EDGE,{"derivedFrom":sQuery(id+"F2.wireOp",EDGE,"E165.MirrorC")})}),1.0]])]});
            var Q258;
            Q258=makeQuery(id+"F3.imprint","IMPRINT",FACE,{"disambiguationData":[TD([[makeQuery(id+"F3.imprint","IMPRINT",EDGE,{"derivedFrom":makeQuery(id+"F2.imprint","IMPRINT",EDGE,{"derivedFrom":sQuery(id+"F2.wireOp",EDGE,"E139.MirrorC")})}),-1.0]])]});
            var Q259;
            Q259=makeQuery(id+"F3.imprint","IMPRINT",FACE,{"disambiguationData":[TD([[makeQuery(id+"F3.imprint","IMPRINT",EDGE,{"derivedFrom":makeQuery(id+"F2.imprint","IMPRINT",EDGE,{"derivedFrom":sQuery(id+"F2.wireOp",EDGE,"E138.MirrorC")})}),-1.0]])]});
            var Q260;
            Q260=makeQuery(id+"F3.imprint","IMPRINT",FACE,{"disambiguationData":[TD([[makeQuery(id+"F3.imprint","IMPRINT",EDGE,{"derivedFrom":makeQuery(id+"F2.imprint","IMPRINT",EDGE,{"derivedFrom":sQuery(id+"F2.wireOp",EDGE,"E137.MirrorC")})}),-1.0]])]});
            var Q261;
            Q261=makeQuery(id+"F3.imprint","IMPRINT",FACE,{"disambiguationData":[TD([[makeQuery(id+"F3.imprint","IMPRINT",EDGE,{"derivedFrom":makeQuery(id+"F2.imprint","IMPRINT",EDGE,{"derivedFrom":sQuery(id+"F2.wireOp",EDGE,"E134.MirrorC")})}),-1.0]])]});
            var Q262;
            Q262=makeQuery(id+"F3.imprint","IMPRINT",FACE,{"disambiguationData":[TD([[makeQuery(id+"F3.imprint","IMPRINT",EDGE,{"derivedFrom":makeQuery(id+"F2.imprint","IMPRINT",EDGE,{"derivedFrom":sQuery(id+"F2.wireOp",EDGE,"E132.MirrorC")})}),-1.0]])]});
            var Q263;
            Q263=makeQuery(id+"F3.imprint","IMPRINT",FACE,{"disambiguationData":[TD([[makeQuery(id+"F3.imprint","IMPRINT",EDGE,{"derivedFrom":makeQuery(id+"F2.imprint","IMPRINT",EDGE,{"derivedFrom":sQuery(id+"F2.wireOp",EDGE,"E131.MirrorC")})}),-1.0]])]});
            var Q264;
            Q264=makeQuery(id+"F3.imprint","IMPRINT",FACE,{"disambiguationData":[TD([[makeQuery(id+"F3.imprint","IMPRINT",EDGE,{"derivedFrom":makeQuery(id+"F2.imprint","IMPRINT",EDGE,{"derivedFrom":sQuery(id+"F2.wireOp",EDGE,"E130.MirrorC")})}),-1.0]])]});
            var Q265;
            Q265=makeQuery(id+"F3.imprint","IMPRINT",FACE,{"disambiguationData":[TD([[makeQuery(id+"F3.imprint","IMPRINT",EDGE,{"derivedFrom":makeQuery(id+"F2.imprint","IMPRINT",EDGE,{"derivedFrom":sQuery(id+"F2.wireOp",EDGE,"E129.MirrorC")})}),-1.0]])]});
            var Q266;
            Q266=makeQuery(id+"F3.imprint","IMPRINT",FACE,{"disambiguationData":[TD([[makeQuery(id+"F3.imprint","IMPRINT",EDGE,{"derivedFrom":makeQuery(id+"F2.imprint","IMPRINT",EDGE,{"derivedFrom":sQuery(id+"F2.wireOp",EDGE,"E128.MirrorC")})}),-1.0]])]});
            var Q267;
            Q267=makeQuery(id+"F3.imprint","IMPRINT",FACE,{"disambiguationData":[TD([[makeQuery(id+"F3.imprint","IMPRINT",EDGE,{"derivedFrom":makeQuery(id+"F2.imprint","IMPRINT",EDGE,{"derivedFrom":sQuery(id+"F2.wireOp",EDGE,"E126.MirrorC")})}),-1.0]])]});
            var Q268;
            Q268=makeQuery(id+"F3.imprint","IMPRINT",FACE,{"disambiguationData":[TD([[makeQuery(id+"F3.imprint","IMPRINT",EDGE,{"derivedFrom":makeQuery(id+"F2.imprint","IMPRINT",EDGE,{"derivedFrom":sQuery(id+"F2.wireOp",EDGE,"E125.MirrorC")})}),-1.0]])]});
            var Q269;
            Q269=makeQuery(id+"F3.imprint","IMPRINT",FACE,{"disambiguationData":[TD([[makeQuery(id+"F3.imprint","IMPRINT",EDGE,{"derivedFrom":makeQuery(id+"F2.imprint","IMPRINT",EDGE,{"derivedFrom":sQuery(id+"F2.wireOp",EDGE,"E123.MirrorC")})}),-1.0]])]});
            var Q270;
            Q270=makeQuery(id+"F3.imprint","IMPRINT",FACE,{"disambiguationData":[TD([[makeQuery(id+"F3.imprint","IMPRINT",EDGE,{"derivedFrom":makeQuery(id+"F2.imprint","IMPRINT",EDGE,{"derivedFrom":sQuery(id+"F2.wireOp",EDGE,"E121.MirrorC")})}),-1.0]])]});
            var Q271;
            Q271=makeQuery(id+"F3.imprint","IMPRINT",FACE,{"disambiguationData":[TD([[makeQuery(id+"F3.imprint","IMPRINT",EDGE,{"derivedFrom":makeQuery(id+"F2.imprint","IMPRINT",EDGE,{"derivedFrom":sQuery(id+"F2.wireOp",EDGE,"E119.MirrorC")})}),-1.0]])]});
            var Q272;
            Q272=makeQuery(id+"F3.imprint","IMPRINT",FACE,{"disambiguationData":[TD([[makeQuery(id+"F3.imprint","IMPRINT",EDGE,{"derivedFrom":makeQuery(id+"F2.imprint","IMPRINT",EDGE,{"derivedFrom":sQuery(id+"F2.wireOp",EDGE,"E118.MirrorC")})}),-1.0]])]});
            var Q273;
            Q273=makeQuery(id+"F2.imprint","IMPRINT",FACE,{"disambiguationData":[TD([[makeQuery(id+"F2.imprint","IMPRINT",EDGE,{"derivedFrom":sQuery(id+"F2.wireOp",EDGE,"b689cfbc-3e02-4c3a-b580-67513f19e31b32.MirrorCS")}),-1.0]])]});
            var Q274;
            Q274=makeQuery(id+"F2.imprint","IMPRINT",FACE,{"disambiguationData":[TD([[makeQuery(id+"F2.imprint","IMPRINT",EDGE,{"derivedFrom":sQuery(id+"F2.wireOp",EDGE,"b689cfbc-3e02-4c3a-b580-67513f19e31b5.MirrorCS")}),-1.0]])]});
            var Q275;
            Q275=makeQuery(id+"F2.imprint","IMPRINT",FACE,{"disambiguationData":[TD([[makeQuery(id+"F2.imprint","IMPRINT",EDGE,{"derivedFrom":sQuery(id+"F2.wireOp",EDGE,"b689cfbc-3e02-4c3a-b580-67513f19e31b41.MirrorCS")}),1.0]])]});
            var Q276;
            Q276=makeQuery(id+"F3.imprint","IMPRINT",FACE,{"disambiguationData":[TD([[makeQuery(id+"F3.imprint","IMPRINT",EDGE,{"derivedFrom":makeQuery(id+"F2.imprint","IMPRINT",EDGE,{"derivedFrom":sQuery(id+"F2.wireOp",EDGE,"b689cfbc-3e02-4c3a-b580-67513f19e31b32.MirrorCS")})}),-1.0]])]});
            var Q277;
            Q277=makeQuery(id+"F2.imprint","IMPRINT",FACE,{"disambiguationData":[TD([[makeQuery(id+"F2.imprint","IMPRINT",EDGE,{"derivedFrom":sQuery(id+"F2.wireOp",EDGE,"b689cfbc-3e02-4c3a-b580-67513f19e31b2.MirrorCS")}),-1.0]])]});
            var Q278;
            Q278=makeQuery(id+"F2.imprint","IMPRINT",FACE,{"disambiguationData":[TD([[makeQuery(id+"F2.imprint","IMPRINT",EDGE,{"derivedFrom":sQuery(id+"F2.wireOp",EDGE,"b689cfbc-3e02-4c3a-b580-67513f19e31b34.MirrorCS")}),1.0]])]});
            var Q279;
            Q279=makeQuery(id+"F2.imprint","IMPRINT",FACE,{"disambiguationData":[TD([[makeQuery(id+"F2.imprint","IMPRINT",EDGE,{"derivedFrom":sQuery(id+"F2.wireOp",EDGE,"b689cfbc-3e02-4c3a-b580-67513f19e31b7.MirrorCS")}),-1.0]])]});
            var Q280;
            Q280=makeQuery(id+"F2.imprint","IMPRINT",FACE,{"disambiguationData":[TD([[makeQuery(id+"F2.imprint","IMPRINT",EDGE,{"derivedFrom":sQuery(id+"F2.wireOp",EDGE,"b689cfbc-3e02-4c3a-b580-67513f19e31b38.MirrorCS")}),1.0]])]});
            var Q281;
            Q281=makeQuery(id+"F2.imprint","IMPRINT",FACE,{"disambiguationData":[TD([[makeQuery(id+"F2.imprint","IMPRINT",EDGE,{"derivedFrom":sQuery(id+"F2.wireOp",EDGE,"b689cfbc-3e02-4c3a-b580-67513f19e31b36.MirrorCS")}),1.0]])]});
            var Q282;
            Q282=makeQuery(id+"F2.imprint","IMPRINT",FACE,{"disambiguationData":[TD([[makeQuery(id+"F2.imprint","IMPRINT",EDGE,{"derivedFrom":sQuery(id+"F2.wireOp",EDGE,"b689cfbc-3e02-4c3a-b580-67513f19e31b31.MirrorCS")}),1.0]])]});
            var Q283;
            Q283=makeQuery(id+"F2.imprint","IMPRINT",FACE,{"disambiguationData":[TD([[makeQuery(id+"F2.imprint","IMPRINT",EDGE,{"derivedFrom":sQuery(id+"F2.wireOp",EDGE,"b689cfbc-3e02-4c3a-b580-67513f19e31b37.MirrorCS")}),-1.0]])]});
            var Q284;
            Q284=makeQuery(id+"F2.imprint","IMPRINT",FACE,{"disambiguationData":[TD([[makeQuery(id+"F2.imprint","IMPRINT",EDGE,{"derivedFrom":sQuery(id+"F2.wireOp",EDGE,"b689cfbc-3e02-4c3a-b580-67513f19e31b4.MirrorCS")}),-1.0]])]});
            var Q285;
            Q285=makeQuery(id+"F3.imprint","IMPRINT",FACE,{"disambiguationData":[TD([[makeQuery(id+"F3.imprint","IMPRINT",EDGE,{"derivedFrom":makeQuery(id+"F2.imprint","IMPRINT",EDGE,{"derivedFrom":sQuery(id+"F2.wireOp",EDGE,"b689cfbc-3e02-4c3a-b580-67513f19e31b7.MirrorCS")})}),-1.0]])]});
            var Q286;
            Q286=makeQuery(id+"F3.imprint","IMPRINT",FACE,{"disambiguationData":[TD([[makeQuery(id+"F3.imprint","IMPRINT",EDGE,{"derivedFrom":makeQuery(id+"F2.imprint","IMPRINT",EDGE,{"derivedFrom":sQuery(id+"F2.wireOp",EDGE,"b689cfbc-3e02-4c3a-b580-67513f19e31b34.MirrorCS")})}),1.0]])]});
            var Q287;
            Q287=makeQuery(id+"F3.imprint","IMPRINT",FACE,{"disambiguationData":[TD([[makeQuery(id+"F3.imprint","IMPRINT",EDGE,{"derivedFrom":makeQuery(id+"F2.imprint","IMPRINT",EDGE,{"derivedFrom":sQuery(id+"F2.wireOp",EDGE,"b689cfbc-3e02-4c3a-b580-67513f19e31b36.MirrorCS")})}),1.0]])]});
            var Q288;
            Q288=makeQuery(id+"F3.imprint","IMPRINT",FACE,{"disambiguationData":[TD([[makeQuery(id+"F3.imprint","IMPRINT",EDGE,{"derivedFrom":makeQuery(id+"F2.imprint","IMPRINT",EDGE,{"derivedFrom":sQuery(id+"F2.wireOp",EDGE,"b689cfbc-3e02-4c3a-b580-67513f19e31b5.MirrorCS")})}),-1.0]])]});
            var Q289;
            Q289=makeQuery(id+"F3.imprint","IMPRINT",FACE,{"disambiguationData":[TD([[makeQuery(id+"F3.imprint","IMPRINT",EDGE,{"derivedFrom":makeQuery(id+"F2.imprint","IMPRINT",EDGE,{"derivedFrom":sQuery(id+"F2.wireOp",EDGE,"b689cfbc-3e02-4c3a-b580-67513f19e31b41.MirrorCS")})}),1.0]])]});
            var Q290;
            Q290=makeQuery(id+"F3.imprint","IMPRINT",FACE,{"disambiguationData":[TD([[makeQuery(id+"F3.imprint","IMPRINT",EDGE,{"derivedFrom":makeQuery(id+"F2.imprint","IMPRINT",EDGE,{"derivedFrom":sQuery(id+"F2.wireOp",EDGE,"b689cfbc-3e02-4c3a-b580-67513f19e31b4.MirrorCS")})}),-1.0]])]});
            var Q291;
            Q291=makeQuery(id+"F3.imprint","IMPRINT",FACE,{"disambiguationData":[TD([[makeQuery(id+"F3.imprint","IMPRINT",EDGE,{"derivedFrom":makeQuery(id+"F2.imprint","IMPRINT",EDGE,{"derivedFrom":sQuery(id+"F2.wireOp",EDGE,"b689cfbc-3e02-4c3a-b580-67513f19e31b31.MirrorCS")})}),1.0]])]});
            var Q292;
            Q292=makeQuery(id+"F3.imprint","IMPRINT",FACE,{"disambiguationData":[TD([[makeQuery(id+"F3.imprint","IMPRINT",EDGE,{"derivedFrom":makeQuery(id+"F2.imprint","IMPRINT",EDGE,{"derivedFrom":sQuery(id+"F2.wireOp",EDGE,"b689cfbc-3e02-4c3a-b580-67513f19e31b2.MirrorCS")})}),-1.0]])]});
            var Q293;
            Q293=makeQuery(id+"F3.imprint","IMPRINT",FACE,{"disambiguationData":[TD([[makeQuery(id+"F3.imprint","IMPRINT",EDGE,{"derivedFrom":makeQuery(id+"F2.imprint","IMPRINT",EDGE,{"derivedFrom":sQuery(id+"F2.wireOp",EDGE,"b689cfbc-3e02-4c3a-b580-67513f19e31b37.MirrorCS")})}),-1.0]])]});
            var Q294;
            Q294=makeQuery(id+"F3.imprint","IMPRINT",FACE,{"disambiguationData":[TD([[makeQuery(id+"F3.imprint","IMPRINT",EDGE,{"derivedFrom":makeQuery(id+"F2.imprint","IMPRINT",EDGE,{"derivedFrom":sQuery(id+"F2.wireOp",EDGE,"b689cfbc-3e02-4c3a-b580-67513f19e31b38.MirrorCS")})}),1.0]])]});
            var Q295;
            Q295=makeQuery(id+"F2.imprint","IMPRINT",FACE,{"disambiguationData":[TD([[makeQuery(id+"F2.imprint","IMPRINT",EDGE,{"derivedFrom":sQuery(id+"F2.wireOp",EDGE,"b689cfbc-3e02-4c3a-b580-67513f19e31b21.MirrorCS")}),1.0]])]});
            var Q296;
            Q296=makeQuery(id+"F3.imprint","IMPRINT",FACE,{"disambiguationData":[TD([[makeQuery(id+"F3.imprint","IMPRINT",EDGE,{"derivedFrom":makeQuery(id+"F2.imprint","IMPRINT",EDGE,{"derivedFrom":sQuery(id+"F2.wireOp",EDGE,"b689cfbc-3e02-4c3a-b580-67513f19e31b21.MirrorCS")})}),1.0]])]});
            var Q297;
            Q297=makeQuery(id+"F2.imprint","IMPRINT",FACE,{"disambiguationData":[TD([[makeQuery(id+"F2.imprint","IMPRINT",EDGE,{"derivedFrom":sQuery(id+"F2.wireOp",EDGE,"E216.MirrorCS")}),-1.0]])]});
            var Q298;
            Q298=makeQuery(id+"F2.imprint","IMPRINT",FACE,{"disambiguationData":[TD([[makeQuery(id+"F2.imprint","IMPRINT",EDGE,{"derivedFrom":sQuery(id+"F2.wireOp",EDGE,"E228.MirrorCS")}),1.0]])]});
            var Q299;
            Q299=makeQuery(id+"F2.imprint","IMPRINT",FACE,{"disambiguationData":[TD([[makeQuery(id+"F2.imprint","IMPRINT",EDGE,{"derivedFrom":sQuery(id+"F2.wireOp",EDGE,"E188.MirrorCS")}),1.0]])]});
            var Q300;
            Q300=makeQuery(id+"F2.imprint","IMPRINT",FACE,{"disambiguationData":[TD([[makeQuery(id+"F2.imprint","IMPRINT",EDGE,{"derivedFrom":sQuery(id+"F2.wireOp",EDGE,"E195.MirrorCS")}),-1.0]])]});
            var Q301;
            Q301=makeQuery(id+"F2.imprint","IMPRINT",FACE,{"disambiguationData":[TD([[makeQuery(id+"F2.imprint","IMPRINT",EDGE,{"derivedFrom":sQuery(id+"F2.wireOp",EDGE,"E213.MirrorCS")}),1.0]])]});
            var Q302;
            Q302=makeQuery(id+"F2.imprint","IMPRINT",FACE,{"disambiguationData":[TD([[makeQuery(id+"F2.imprint","IMPRINT",EDGE,{"derivedFrom":sQuery(id+"F2.wireOp",EDGE,"E212.MirrorCS")}),1.0]])]});
            var Q303;
            Q303=makeQuery(id+"F2.imprint","IMPRINT",FACE,{"disambiguationData":[TD([[makeQuery(id+"F2.imprint","IMPRINT",EDGE,{"derivedFrom":sQuery(id+"F2.wireOp",EDGE,"E214.MirrorCS")}),-1.0]])]});
            var Q304;
            Q304=makeQuery(id+"F2.imprint","IMPRINT",FACE,{"disambiguationData":[TD([[makeQuery(id+"F2.imprint","IMPRINT",EDGE,{"derivedFrom":sQuery(id+"F2.wireOp",EDGE,"E48.MirrorCS")}),1.0]])]});
            var Q305;
            Q305=makeQuery(id+"F2.imprint","IMPRINT",FACE,{"disambiguationData":[TD([[makeQuery(id+"F2.imprint","IMPRINT",EDGE,{"derivedFrom":sQuery(id+"F2.wireOp",EDGE,"E211.MirrorCS")}),-1.0]])]});
            var Q306;
            Q306=makeQuery(id+"F2.imprint","IMPRINT",FACE,{"disambiguationData":[TD([[makeQuery(id+"F2.imprint","IMPRINT",EDGE,{"derivedFrom":sQuery(id+"F2.wireOp",EDGE,"E189.MirrorCS")}),1.0]])]});
            var Q307;
            Q307=makeQuery(id+"F2.imprint","IMPRINT",FACE,{"disambiguationData":[TD([[makeQuery(id+"F2.imprint","IMPRINT",EDGE,{"derivedFrom":sQuery(id+"F2.wireOp",EDGE,"E261.MirrorCS")}),1.0]])]});
            var Q308;
            Q308=makeQuery(id+"F2.imprint","IMPRINT",FACE,{"disambiguationData":[TD([[makeQuery(id+"F2.imprint","IMPRINT",EDGE,{"derivedFrom":sQuery(id+"F2.wireOp",EDGE,"E267.MirrorCS")}),1.0]])]});
            var Q309;
            Q309=makeQuery(id+"F2.imprint","IMPRINT",FACE,{"disambiguationData":[TD([[makeQuery(id+"F2.imprint","IMPRINT",EDGE,{"derivedFrom":sQuery(id+"F2.wireOp",EDGE,"E262.MirrorCS")}),-1.0]])]});
            var Q310;
            Q310=makeQuery(id+"F2.imprint","IMPRINT",FACE,{"disambiguationData":[TD([[makeQuery(id+"F2.imprint","IMPRINT",EDGE,{"derivedFrom":sQuery(id+"F2.wireOp",EDGE,"E265.MirrorCS")}),1.0]])]});
            var Q311;
            Q311=makeQuery(id+"F2.imprint","IMPRINT",FACE,{"disambiguationData":[TD([[makeQuery(id+"F2.imprint","IMPRINT",EDGE,{"derivedFrom":sQuery(id+"F2.wireOp",EDGE,"E294.MirrorCS")}),-1.0]])]});
            var Q312;
            Q312=makeQuery(id+"F2.imprint","IMPRINT",FACE,{"disambiguationData":[TD([[makeQuery(id+"F2.imprint","IMPRINT",EDGE,{"derivedFrom":sQuery(id+"F2.wireOp",EDGE,"E303.MirrorCS")}),1.0]])]});
            var Q313;
            Q313=makeQuery(id+"F2.imprint","IMPRINT",FACE,{"disambiguationData":[TD([[makeQuery(id+"F2.imprint","IMPRINT",EDGE,{"derivedFrom":sQuery(id+"F2.wireOp",EDGE,"E260.MirrorCS")}),1.0]])]});
            var Q314;
            Q314=makeQuery(id+"F2.imprint","IMPRINT",FACE,{"disambiguationData":[TD([[makeQuery(id+"F2.imprint","IMPRINT",EDGE,{"derivedFrom":sQuery(id+"F2.wireOp",EDGE,"E295.MirrorCS")}),1.0]])]});
            var Q315;
            Q315=makeQuery(id+"F2.imprint","IMPRINT",FACE,{"disambiguationData":[TD([[makeQuery(id+"F2.imprint","IMPRINT",EDGE,{"derivedFrom":sQuery(id+"F2.wireOp",EDGE,"E259.MirrorCS")}),-1.0]])]});
            var Q316;
            Q316=makeQuery(id+"F2.imprint","IMPRINT",FACE,{"disambiguationData":[TD([[makeQuery(id+"F2.imprint","IMPRINT",EDGE,{"derivedFrom":sQuery(id+"F2.wireOp",EDGE,"E257.MirrorCS")}),1.0]])]});
            var Q317;
            Q317=makeQuery(id+"F2.imprint","IMPRINT",FACE,{"disambiguationData":[TD([[makeQuery(id+"F2.imprint","IMPRINT",EDGE,{"derivedFrom":sQuery(id+"F2.wireOp",EDGE,"E264.MirrorCS")}),-1.0]])]});
            var Q318;
            Q318=makeQuery(id+"F2.imprint","IMPRINT",FACE,{"disambiguationData":[TD([[makeQuery(id+"F2.imprint","IMPRINT",EDGE,{"derivedFrom":sQuery(id+"F2.wireOp",EDGE,"E256.MirrorCS")}),1.0]])]});
            extrude(context, id + "F4", {"entities" : qUnion([Q0, Q1, Q2, Q3, Q4, Q5, Q6, Q7, Q8, Q9, Q10, Q11, Q12, Q13, Q14, Q15, Q16, Q17, Q18, Q19, Q20, Q21, Q22, Q23, Q24, Q25, Q26, Q27, Q28, Q29, Q30, Q31, Q32, Q33, Q34, Q35, Q36, Q37, Q38, Q39, Q40, Q41, Q42, Q43, Q44, Q45, Q46, Q47, Q48, Q49, Q50, Q51, Q52, Q53, Q54, Q55, Q56, Q57, Q58, Q59, Q60, Q61, Q62, Q63, Q64, Q65, Q66, Q67, Q68, Q69, Q70, Q71, Q72, Q73, Q74, Q75, Q76, Q77, Q78, Q79, Q80, Q81, Q82, Q83, Q84, Q85, Q86, Q87, Q88, Q89, Q90, Q91, Q92, Q93, Q94, Q95, Q96, Q97, Q98, Q99, Q100, Q101, Q102, Q103, Q104, Q105, Q106, Q107, Q108, Q109, Q110, Q111, Q112, Q113, Q114, Q115, Q116, Q117, Q118, Q119, Q120, Q121, Q122, Q123, Q124, Q125, Q126, Q127, Q128, Q129, Q130, Q131, Q132, Q133, Q134, Q135, Q136, Q137, Q138, Q139, Q140, Q141, Q142, Q143, Q144, Q145, Q146, Q147, Q148, Q149, Q150, Q151, Q152, Q153, Q154, Q155, Q156, Q157, Q158, Q159, Q160, Q161, Q162, Q163, Q164, Q165, Q166, Q167, Q168, Q169, Q170, Q171, Q172, Q173, Q174, Q175, Q176, Q177, Q178, Q179, Q180, Q181, Q182, Q183, Q184, Q185, Q186, Q187, Q188, Q189, Q190, Q191, Q192, Q193, Q194, Q195, Q196, Q197, Q198, Q199, Q200, Q201, Q202, Q203, Q204, Q205, Q206, Q207, Q208, Q209, Q210, Q211, Q212, Q213, Q214, Q215, Q216, Q217, Q218, Q219, Q220, Q221, Q222, Q223, Q224, Q225, Q226, Q227, Q228, Q229, Q230, Q231, Q232, Q233, Q234, Q235, Q236, Q237, Q238, Q239, Q240, Q241, Q242, Q243, Q244, Q245, Q246, Q247, Q248, Q249, Q250, Q251, Q252, Q253, Q254, Q255, Q256, Q257, Q258, Q259, Q260, Q261, Q262, Q263, Q264, Q265, Q266, Q267, Q268, Q269, Q270, Q271, Q272, Q273, Q274, Q275, Q276, Q277, Q278, Q279, Q280, Q281, Q282, Q283, Q284, Q285, Q286, Q287, Q288, Q289, Q290, Q291, Q292, Q293, Q294, Q295, Q296, Q297, Q298, Q299, Q300, Q301, Q302, Q303, Q304, Q305, Q306, Q307, Q308, Q309, Q310, Q311, Q312, Q313, Q314, Q315, Q316, Q317, Q318]), "operationType" : NewBodyOperationType.REMOVE, "flatOperationType" : FlatOperationType.REMOVE, "oppositeDirection" : true, "depth" : 3 * mm, "offsetDistance" : 25 * mm, "domain" : OperationDomain.MODEL});
        }
    });
